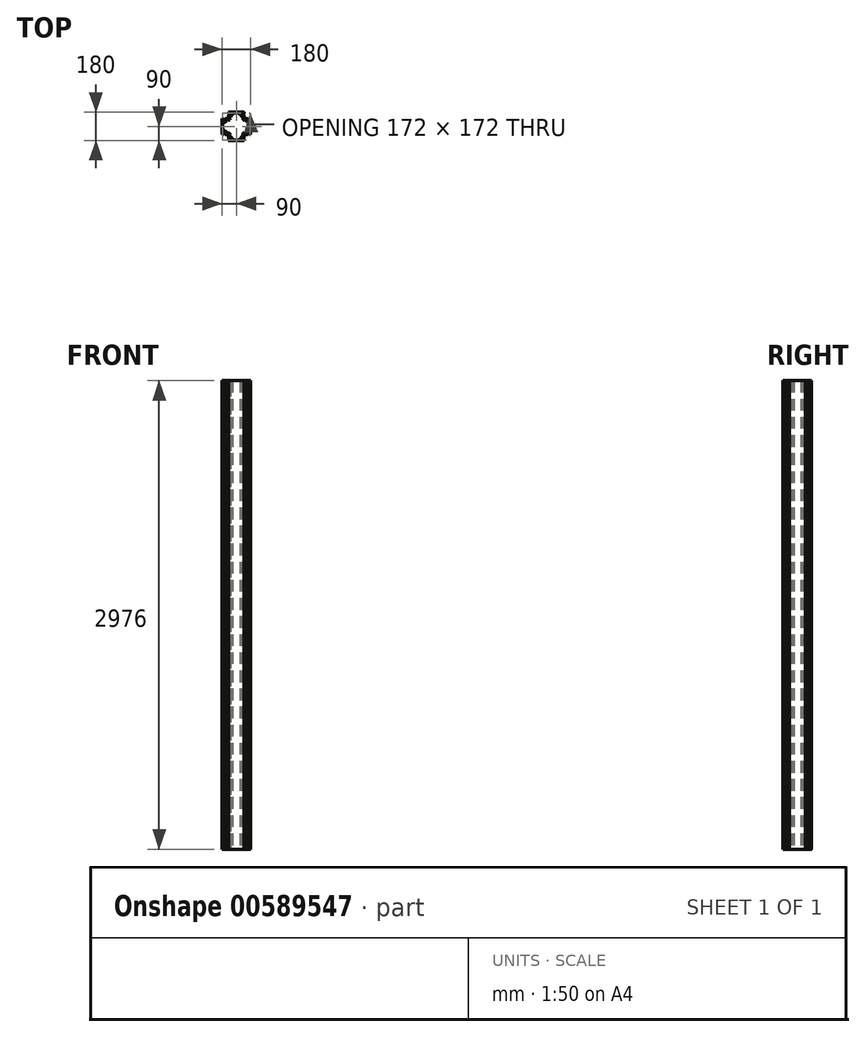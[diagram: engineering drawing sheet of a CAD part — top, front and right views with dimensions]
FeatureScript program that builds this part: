
annotation { "Feature Type Name" : "Feature", "Feature Type Description" : "" }
export const myFeature = defineFeature(function(context is Context, id is Id, definition is map)
    precondition{}
    {
        {
            var Q0;
            Q0=qCreatedBy(makeId("Top.planeOp"),FACE);
            var sketch = newSketch(context, id + "F0", { "sketchPlane" : qUnion([Q0])});
            skLineSegment(sketch, "E0", {"start": v(-58.4, 0) * mm, "end": v(68.52, 0) * mm, "construction": true});
            skLineSegment(sketch, "E1", {"start": v(0, 55.81) * mm, "end": v(0, -52.18) * mm, "construction": true});
            skLineSegment(sketch, "E2.bottom", {"start": v(-50, 90) * mm, "end": v(50, 90) * mm});
            skLineSegment(sketch, "E2.top", {"start": v(-50, -90) * mm, "end": v(50, -90) * mm});
            skLineSegment(sketch, "E2.left", {"start": v(-90, 50) * mm, "end": v(-90, -50) * mm});
            skLineSegment(sketch, "E2.right", {"start": v(90, 50) * mm, "end": v(90, -50) * mm});
            skLineSegment(sketch, "E3", {"start": v(-90, 50) * mm, "end": v(-82, 50) * mm});
            skLineSegment(sketch, "E4", {"start": v(-50, 50) * mm, "end": v(-50, 72) * mm});
            skLineSegment(sketch, "E5.MirrorCS", {"start": v(90, 50) * mm, "end": v(82, 50) * mm});
            skLineSegment(sketch, "E6.MirrorCS", {"start": v(50, 50) * mm, "end": v(50, 72) * mm});
            skLineSegment(sketch, "E7.MirrorCS", {"start": v(50, -50) * mm, "end": v(50, -72) * mm});
            skLineSegment(sketch, "E8.MirrorCS", {"start": v(90, -50) * mm, "end": v(82, -50) * mm});
            skLineSegment(sketch, "E9.MirrorCS", {"start": v(-50, -50) * mm, "end": v(-50, -72) * mm});
            skLineSegment(sketch, "E10.MirrorCS", {"start": v(-90, -50) * mm, "end": v(-82, -50) * mm});
            skLineSegment(sketch, "E11", {"start": v(-82, -50) * mm, "end": v(-82, -46) * mm});
            skLineSegment(sketch, "E12", {"start": v(-82, -46) * mm, "end": v(-86, -46) * mm});
            skLineSegment(sketch, "E13", {"start": v(-86, -46) * mm, "end": v(-86, -38) * mm});
            skLineSegment(sketch, "E14", {"start": v(-86, -38) * mm, "end": v(-68, -38) * mm});
            skLineSegment(sketch, "E15", {"start": v(-68, -38) * mm, "end": v(-68, -46) * mm});
            skLineSegment(sketch, "E16", {"start": v(-68, -46) * mm, "end": v(-72, -46) * mm});
            skLineSegment(sketch, "E17", {"start": v(-72, -46) * mm, "end": v(-72, -50) * mm});
            skLineSegment(sketch, "E18.MirrorCS", {"start": v(-68, 46) * mm, "end": v(-72, 46) * mm});
            skLineSegment(sketch, "E19.MirrorCS", {"start": v(-86, 38) * mm, "end": v(-68, 38) * mm});
            skLineSegment(sketch, "E20.MirrorCS", {"start": v(-82, 50) * mm, "end": v(-82, 46) * mm});
            skLineSegment(sketch, "E21.MirrorCS", {"start": v(-86, 46) * mm, "end": v(-86, 38) * mm});
            skLineSegment(sketch, "E22.MirrorCS", {"start": v(-82, 46) * mm, "end": v(-86, 46) * mm});
            skLineSegment(sketch, "E23.MirrorCS", {"start": v(-68, 38) * mm, "end": v(-68, 46) * mm});
            skLineSegment(sketch, "E24.MirrorCS", {"start": v(-72, 46) * mm, "end": v(-72, 50) * mm});
            skLineSegment(sketch, "E25.MirrorCS", {"start": v(68, -38) * mm, "end": v(68, -46) * mm});
            skLineSegment(sketch, "E26.MirrorCS", {"start": v(86, 38) * mm, "end": v(68, 38) * mm});
            skLineSegment(sketch, "E27.MirrorCS", {"start": v(82, 46) * mm, "end": v(86, 46) * mm});
            skLineSegment(sketch, "E28.MirrorCS", {"start": v(86, -38) * mm, "end": v(68, -38) * mm});
            skLineSegment(sketch, "E29.MirrorCS", {"start": v(68, 46) * mm, "end": v(72, 46) * mm});
            skLineSegment(sketch, "E30.MirrorCS", {"start": v(86, 46) * mm, "end": v(86, 38) * mm});
            skLineSegment(sketch, "E31.MirrorCS", {"start": v(86, -46) * mm, "end": v(86, -38) * mm});
            skLineSegment(sketch, "E32.MirrorCS", {"start": v(72, -46) * mm, "end": v(72, -50) * mm});
            skLineSegment(sketch, "E33.MirrorCS", {"start": v(82, 50) * mm, "end": v(82, 46) * mm});
            skLineSegment(sketch, "E34.MirrorCS", {"start": v(72, 46) * mm, "end": v(72, 50) * mm});
            skLineSegment(sketch, "E35.MirrorCS", {"start": v(68, 38) * mm, "end": v(68, 46) * mm});
            skLineSegment(sketch, "E36.MirrorCS", {"start": v(82, -50) * mm, "end": v(82, -46) * mm});
            skLineSegment(sketch, "E37.MirrorCS", {"start": v(68, -46) * mm, "end": v(72, -46) * mm});
            skLineSegment(sketch, "E38.MirrorCS", {"start": v(82, -46) * mm, "end": v(86, -46) * mm});
            skLineSegment(sketch, "E39", {"start": v(-50, 50) * mm, "end": v(0, 0) * mm, "construction": true});
            skLineSegment(sketch, "E40.MirrorCS", {"start": v(-38, 68) * mm, "end": v(-46, 68) * mm});
            skLineSegment(sketch, "E41.MirrorCS", {"start": v(-46, 68) * mm, "end": v(-46, 72) * mm});
            skLineSegment(sketch, "E42.MirrorCS", {"start": v(-46, 72) * mm, "end": v(-50, 72) * mm});
            skLineSegment(sketch, "E43.MirrorCS", {"start": v(-38, 86) * mm, "end": v(-38, 68) * mm});
            skLineSegment(sketch, "E44.MirrorCS", {"start": v(-46, 86) * mm, "end": v(-38, 86) * mm});
            skLineSegment(sketch, "E45.MirrorCS", {"start": v(-50, 82) * mm, "end": v(-46, 82) * mm});
            skLineSegment(sketch, "E46.MirrorCS", {"start": v(-46, 82) * mm, "end": v(-46, 86) * mm});
            skLineSegment(sketch, "E47.MirrorCS", {"start": v(46, 82) * mm, "end": v(46, 86) * mm});
            skLineSegment(sketch, "E48.MirrorCS", {"start": v(38, 86) * mm, "end": v(38, 68) * mm});
            skLineSegment(sketch, "E49.MirrorCS", {"start": v(46, 68) * mm, "end": v(46, 72) * mm});
            skLineSegment(sketch, "E50.MirrorCS", {"start": v(50, 82) * mm, "end": v(46, 82) * mm});
            skLineSegment(sketch, "E51.MirrorCS", {"start": v(46, 86) * mm, "end": v(38, 86) * mm});
            skLineSegment(sketch, "E52.MirrorCS", {"start": v(38, 68) * mm, "end": v(46, 68) * mm});
            skLineSegment(sketch, "E53.MirrorCS", {"start": v(46, 72) * mm, "end": v(50, 72) * mm});
            skLineSegment(sketch, "E54.MirrorCS", {"start": v(-46, -86) * mm, "end": v(-38, -86) * mm});
            skLineSegment(sketch, "E55.MirrorCS", {"start": v(50, -82) * mm, "end": v(46, -82) * mm});
            skLineSegment(sketch, "E56.MirrorCS", {"start": v(-38, -86) * mm, "end": v(-38, -68) * mm});
            skLineSegment(sketch, "E57.MirrorCS", {"start": v(-46, -82) * mm, "end": v(-46, -86) * mm});
            skLineSegment(sketch, "E58.MirrorCS", {"start": v(-38, -68) * mm, "end": v(-46, -68) * mm});
            skLineSegment(sketch, "E59.MirrorCS", {"start": v(38, -86) * mm, "end": v(38, -68) * mm});
            skLineSegment(sketch, "E60.MirrorCS", {"start": v(-50, -82) * mm, "end": v(-46, -82) * mm});
            skLineSegment(sketch, "E61.MirrorCS", {"start": v(-46, -72) * mm, "end": v(-50, -72) * mm});
            skLineSegment(sketch, "E62.MirrorCS", {"start": v(-46, -68) * mm, "end": v(-46, -72) * mm});
            skLineSegment(sketch, "E63.MirrorCS", {"start": v(46, -72) * mm, "end": v(50, -72) * mm});
            skLineSegment(sketch, "E64.MirrorCS", {"start": v(38, -68) * mm, "end": v(46, -68) * mm});
            skLineSegment(sketch, "E65.MirrorCS", {"start": v(46, -68) * mm, "end": v(46, -72) * mm});
            skLineSegment(sketch, "E66.MirrorCS", {"start": v(46, -82) * mm, "end": v(46, -86) * mm});
            skLineSegment(sketch, "E67.MirrorCS", {"start": v(46, -86) * mm, "end": v(38, -86) * mm});
            skLineSegment(sketch, "E68.trimOffspring", {"start": v(-72, 50) * mm, "end": v(-50, 50) * mm});
            skLineSegment(sketch, "E69.trimOffspring", {"start": v(-50, 82) * mm, "end": v(-50, 90) * mm});
            skLineSegment(sketch, "E70.trimOffspring", {"start": v(50, 82) * mm, "end": v(50, 90) * mm});
            skLineSegment(sketch, "E71.trimOffspring", {"start": v(72, 50) * mm, "end": v(50, 50) * mm});
            skLineSegment(sketch, "E72.trimOffspring", {"start": v(72, -50) * mm, "end": v(50, -50) * mm});
            skLineSegment(sketch, "E73.trimOffspring", {"start": v(50, -82) * mm, "end": v(50, -90) * mm});
            skLineSegment(sketch, "E74.trimOffspring", {"start": v(-50, -82) * mm, "end": v(-50, -90) * mm});
            skLineSegment(sketch, "E75.trimOffspring", {"start": v(-72, -50) * mm, "end": v(-50, -50) * mm});
            skSolve(sketch);
        }
        {
            var Q0;
            Q0=qSketchRegion(id+"F0",true);
            extrude(context, id + "F1", {"entities" : qUnion([Q0]), "depth" : 2976 * mm, "offsetDistance" : 25 * mm});
        }
        {
            var Q0;
            Q0=makeQuery(id+"F1.opExtrude","CAP_FACE",FACE,{"disambiguationData":[OSD([sQuery(id+"F0.wireOp",EDGE,"E2.bottom"),sQuery(id+"F0.wireOp",EDGE,"E2.top"),sQuery(id+"F0.wireOp",EDGE,"E2.left"),sQuery(id+"F0.wireOp",EDGE,"E2.right"),sQuery(id+"F0.wireOp",EDGE,"E3"),sQuery(id+"F0.wireOp",EDGE,"E4"),sQuery(id+"F0.wireOp",EDGE,"E5.MirrorCS"),sQuery(id+"F0.wireOp",EDGE,"E6.MirrorCS"),sQuery(id+"F0.wireOp",EDGE,"E7.MirrorCS"),sQuery(id+"F0.wireOp",EDGE,"E8.MirrorCS"),sQuery(id+"F0.wireOp",EDGE,"E9.MirrorCS"),sQuery(id+"F0.wireOp",EDGE,"E10.MirrorCS")])],"isStart":false});
            var Q1;
            Q1=makeQuery(id+"F1.opExtrude","CAP_FACE",FACE,{"disambiguationData":[OSD([sQuery(id+"F0.wireOp",EDGE,"E2.bottom"),sQuery(id+"F0.wireOp",EDGE,"E2.top"),sQuery(id+"F0.wireOp",EDGE,"E2.left"),sQuery(id+"F0.wireOp",EDGE,"E2.right"),sQuery(id+"F0.wireOp",EDGE,"E3"),sQuery(id+"F0.wireOp",EDGE,"E4"),sQuery(id+"F0.wireOp",EDGE,"E5.MirrorCS"),sQuery(id+"F0.wireOp",EDGE,"E6.MirrorCS"),sQuery(id+"F0.wireOp",EDGE,"E7.MirrorCS"),sQuery(id+"F0.wireOp",EDGE,"E8.MirrorCS"),sQuery(id+"F0.wireOp",EDGE,"E9.MirrorCS"),sQuery(id+"F0.wireOp",EDGE,"E10.MirrorCS")])],"isStart":true});
            shell(context, id + "F2", {"entities" : qUnion([Q0, Q1]), "thickness" : 4 * mm});
        }
        {
            var Q0;
            Q0=makeQuery(id+"F1.opExtrude","SWEPT_EDGE",EDGE,{"disambiguationData":[OSD([sQuery(id+"F0.wireOp",EDGE,"E2.top"),sQuery(id+"F0.wireOp",EDGE,"E74.trimOffspring")])]});
            var Q1;
            Q1=makeQuery(id+"F1.opExtrude","SWEPT_EDGE",EDGE,{"disambiguationData":[OSD([sQuery(id+"F0.wireOp",EDGE,"E2.left"),sQuery(id+"F0.wireOp",EDGE,"E10.MirrorCS")])]});
            var Q2;
            Q2=makeQuery(id+"F1.opExtrude","SWEPT_EDGE",EDGE,{"disambiguationData":[OSD([sQuery(id+"F0.wireOp",EDGE,"E2.top"),sQuery(id+"F0.wireOp",EDGE,"E73.trimOffspring")])]});
            var Q3;
            Q3=makeQuery(id+"F1.opExtrude","SWEPT_EDGE",EDGE,{"disambiguationData":[OSD([sQuery(id+"F0.wireOp",EDGE,"E2.right"),sQuery(id+"F0.wireOp",EDGE,"E8.MirrorCS")])]});
            var Q4;
            Q4=makeQuery(id+"F1.opExtrude","SWEPT_EDGE",EDGE,{"disambiguationData":[OSD([sQuery(id+"F0.wireOp",EDGE,"E2.right"),sQuery(id+"F0.wireOp",EDGE,"E5.MirrorCS")])]});
            var Q5;
            Q5=makeQuery(id+"F1.opExtrude","SWEPT_EDGE",EDGE,{"disambiguationData":[OSD([sQuery(id+"F0.wireOp",EDGE,"E2.bottom"),sQuery(id+"F0.wireOp",EDGE,"E70.trimOffspring")])]});
            var Q6;
            Q6=makeQuery(id+"F1.opExtrude","SWEPT_EDGE",EDGE,{"disambiguationData":[OSD([sQuery(id+"F0.wireOp",EDGE,"E2.bottom"),sQuery(id+"F0.wireOp",EDGE,"E69.trimOffspring")])]});
            var Q7;
            Q7=makeQuery(id+"F1.opExtrude","SWEPT_EDGE",EDGE,{"disambiguationData":[OSD([sQuery(id+"F0.wireOp",EDGE,"E2.left"),sQuery(id+"F0.wireOp",EDGE,"E3")])]});
            fillet(context, id + "F3", {"entities" : qUnion([Q0, Q1, Q2, Q3, Q4, Q5, Q6, Q7]), "radius" : 3 * mm, "tangentPropagation" : true, "allowEdgeOverflow" : false});
        }
        {
            var Q0;
            Q0=makeQuery(id+"F1.opExtrude","CAP_FACE",FACE,{"disambiguationData":[OSD([sQuery(id+"F0.wireOp",EDGE,"E2.bottom"),sQuery(id+"F0.wireOp",EDGE,"E2.top"),sQuery(id+"F0.wireOp",EDGE,"E2.left"),sQuery(id+"F0.wireOp",EDGE,"E2.right"),sQuery(id+"F0.wireOp",EDGE,"E3"),sQuery(id+"F0.wireOp",EDGE,"E4"),sQuery(id+"F0.wireOp",EDGE,"E5.MirrorCS"),sQuery(id+"F0.wireOp",EDGE,"E6.MirrorCS"),sQuery(id+"F0.wireOp",EDGE,"E7.MirrorCS"),sQuery(id+"F0.wireOp",EDGE,"E8.MirrorCS"),sQuery(id+"F0.wireOp",EDGE,"E9.MirrorCS"),sQuery(id+"F0.wireOp",EDGE,"E10.MirrorCS"),sQuery(id+"F0.wireOp",EDGE,"E11"),sQuery(id+"F0.wireOp",EDGE,"E12"),sQuery(id+"F0.wireOp",EDGE,"E13"),sQuery(id+"F0.wireOp",EDGE,"E14"),sQuery(id+"F0.wireOp",EDGE,"E15"),sQuery(id+"F0.wireOp",EDGE,"E16"),sQuery(id+"F0.wireOp",EDGE,"E17"),sQuery(id+"F0.wireOp",EDGE,"E18.MirrorCS"),sQuery(id+"F0.wireOp",EDGE,"E19.MirrorCS"),sQuery(id+"F0.wireOp",EDGE,"E20.MirrorCS"),sQuery(id+"F0.wireOp",EDGE,"E21.MirrorCS"),sQuery(id+"F0.wireOp",EDGE,"E22.MirrorCS"),sQuery(id+"F0.wireOp",EDGE,"E23.MirrorCS"),sQuery(id+"F0.wireOp",EDGE,"E24.MirrorCS"),sQuery(id+"F0.wireOp",EDGE,"E25.MirrorCS"),sQuery(id+"F0.wireOp",EDGE,"E26.MirrorCS"),sQuery(id+"F0.wireOp",EDGE,"E27.MirrorCS"),sQuery(id+"F0.wireOp",EDGE,"E28.MirrorCS"),sQuery(id+"F0.wireOp",EDGE,"E29.MirrorCS"),sQuery(id+"F0.wireOp",EDGE,"E30.MirrorCS"),sQuery(id+"F0.wireOp",EDGE,"E31.MirrorCS"),sQuery(id+"F0.wireOp",EDGE,"E32.MirrorCS"),sQuery(id+"F0.wireOp",EDGE,"E33.MirrorCS"),sQuery(id+"F0.wireOp",EDGE,"E34.MirrorCS"),sQuery(id+"F0.wireOp",EDGE,"E35.MirrorCS"),sQuery(id+"F0.wireOp",EDGE,"E36.MirrorCS"),sQuery(id+"F0.wireOp",EDGE,"E37.MirrorCS"),sQuery(id+"F0.wireOp",EDGE,"E38.MirrorCS"),sQuery(id+"F0.wireOp",EDGE,"E40.MirrorCS"),sQuery(id+"F0.wireOp",EDGE,"E41.MirrorCS"),sQuery(id+"F0.wireOp",EDGE,"E42.MirrorCS"),sQuery(id+"F0.wireOp",EDGE,"E43.MirrorCS"),sQuery(id+"F0.wireOp",EDGE,"E44.MirrorCS"),sQuery(id+"F0.wireOp",EDGE,"E45.MirrorCS"),sQuery(id+"F0.wireOp",EDGE,"E46.MirrorCS"),sQuery(id+"F0.wireOp",EDGE,"E47.MirrorCS"),sQuery(id+"F0.wireOp",EDGE,"E48.MirrorCS"),sQuery(id+"F0.wireOp",EDGE,"E49.MirrorCS"),sQuery(id+"F0.wireOp",EDGE,"E50.MirrorCS"),sQuery(id+"F0.wireOp",EDGE,"E51.MirrorCS"),sQuery(id+"F0.wireOp",EDGE,"E52.MirrorCS"),sQuery(id+"F0.wireOp",EDGE,"E53.MirrorCS"),sQuery(id+"F0.wireOp",EDGE,"E54.MirrorCS"),sQuery(id+"F0.wireOp",EDGE,"E55.MirrorCS"),sQuery(id+"F0.wireOp",EDGE,"E56.MirrorCS"),sQuery(id+"F0.wireOp",EDGE,"E57.MirrorCS"),sQuery(id+"F0.wireOp",EDGE,"E58.MirrorCS"),sQuery(id+"F0.wireOp",EDGE,"E59.MirrorCS"),sQuery(id+"F0.wireOp",EDGE,"E60.MirrorCS"),sQuery(id+"F0.wireOp",EDGE,"E61.MirrorCS"),sQuery(id+"F0.wireOp",EDGE,"E62.MirrorCS"),sQuery(id+"F0.wireOp",EDGE,"E63.MirrorCS"),sQuery(id+"F0.wireOp",EDGE,"E64.MirrorCS"),sQuery(id+"F0.wireOp",EDGE,"E65.MirrorCS"),sQuery(id+"F0.wireOp",EDGE,"E66.MirrorCS"),sQuery(id+"F0.wireOp",EDGE,"E67.MirrorCS"),sQuery(id+"F0.wireOp",EDGE,"E68.trimOffspring"),sQuery(id+"F0.wireOp",EDGE,"E69.trimOffspring"),sQuery(id+"F0.wireOp",EDGE,"E70.trimOffspring"),sQuery(id+"F0.wireOp",EDGE,"E71.trimOffspring"),sQuery(id+"F0.wireOp",EDGE,"E72.trimOffspring"),sQuery(id+"F0.wireOp",EDGE,"E73.trimOffspring"),sQuery(id+"F0.wireOp",EDGE,"E74.trimOffspring"),sQuery(id+"F0.wireOp",EDGE,"E75.trimOffspring")])],"isStart":true});
            var sketch = newSketch(context, id + "F4", { "sketchPlane" : qUnion([Q0])});
            skLineSegment(sketch, "E76.bottom", {"start": v(-64, 38) * mm, "end": v(-61, 38) * mm});
            skLineSegment(sketch, "E76.top", {"start": v(-64, 34) * mm, "end": v(-61, 34) * mm});
            skLineSegment(sketch, "E76.left", {"start": v(-64, 38) * mm, "end": v(-64, 34) * mm});
            skLineSegment(sketch, "E76.right", {"start": v(-61, 38) * mm, "end": v(-61, 34) * mm});
            skLineSegment(sketch, "E77", {"start": v(-74, 34) * mm, "end": v(-74, 23) * mm});
            skLineSegment(sketch, "E78", {"start": v(-74, 23) * mm, "end": v(-78, 23) * mm});
            skLineSegment(sketch, "E79", {"start": v(-78, 23) * mm, "end": v(-78, 34) * mm});
            skLineSegment(sketch, "E80", {"start": v(-78, 34) * mm, "end": v(-74, 34) * mm});
            skLineSegment(sketch, "E81", {"start": v(0, 86) * mm, "end": v(0, 0) * mm, "construction": true});
            skLineSegment(sketch, "E82", {"start": v(0, 0) * mm, "end": v(-86, 0) * mm, "construction": true});
            skLineSegment(sketch, "E83.MirrorCS", {"start": v(64, 38) * mm, "end": v(64, 34) * mm});
            skLineSegment(sketch, "E84.MirrorCS", {"start": v(61, 38) * mm, "end": v(61, 34) * mm});
            skLineSegment(sketch, "E85.MirrorCS", {"start": v(78, 34) * mm, "end": v(74, 34) * mm});
            skLineSegment(sketch, "E86.MirrorCS", {"start": v(74, 23) * mm, "end": v(78, 23) * mm});
            skLineSegment(sketch, "E87.MirrorCS", {"start": v(64, 38) * mm, "end": v(61, 38) * mm});
            skLineSegment(sketch, "E88.MirrorCS", {"start": v(64, 34) * mm, "end": v(61, 34) * mm});
            skLineSegment(sketch, "E89.MirrorCS", {"start": v(78, 23) * mm, "end": v(78, 34) * mm});
            skLineSegment(sketch, "E90.MirrorCS", {"start": v(74, 34) * mm, "end": v(74, 23) * mm});
            skLineSegment(sketch, "E91.MirrorCS", {"start": v(0, 0) * mm, "end": v(86, 0) * mm, "construction": true});
            skLineSegment(sketch, "E92.MirrorCS", {"start": v(74, -34) * mm, "end": v(74, -23) * mm});
            skLineSegment(sketch, "E93.MirrorCS", {"start": v(74, -23) * mm, "end": v(78, -23) * mm});
            skLineSegment(sketch, "E94.MirrorCS", {"start": v(64, -38) * mm, "end": v(61, -38) * mm});
            skLineSegment(sketch, "E95.MirrorCS", {"start": v(64, -34) * mm, "end": v(61, -34) * mm});
            skLineSegment(sketch, "E96.MirrorCS", {"start": v(-64, -38) * mm, "end": v(-61, -38) * mm});
            skLineSegment(sketch, "E97.MirrorCS", {"start": v(-64, -34) * mm, "end": v(-61, -34) * mm});
            skLineSegment(sketch, "E98.MirrorCS", {"start": v(-64, -38) * mm, "end": v(-64, -34) * mm});
            skLineSegment(sketch, "E99.MirrorCS", {"start": v(-61, -38) * mm, "end": v(-61, -34) * mm});
            skLineSegment(sketch, "E100.MirrorCS", {"start": v(-74, -34) * mm, "end": v(-74, -23) * mm});
            skLineSegment(sketch, "E101.MirrorCS", {"start": v(-74, -23) * mm, "end": v(-78, -23) * mm});
            skLineSegment(sketch, "E102.MirrorCS", {"start": v(78, -34) * mm, "end": v(74, -34) * mm});
            skLineSegment(sketch, "E103.MirrorCS", {"start": v(61, -38) * mm, "end": v(61, -34) * mm});
            skLineSegment(sketch, "E104.MirrorCS", {"start": v(78, -23) * mm, "end": v(78, -34) * mm});
            skLineSegment(sketch, "E105.MirrorCS", {"start": v(-78, -34) * mm, "end": v(-74, -34) * mm});
            skLineSegment(sketch, "E106.MirrorCS", {"start": v(-78, -23) * mm, "end": v(-78, -34) * mm});
            skLineSegment(sketch, "E107.MirrorCS", {"start": v(64, -38) * mm, "end": v(64, -34) * mm});
            skLineSegment(sketch, "E108", {"start": v(-46, 46) * mm, "end": v(0, 0) * mm, "construction": true});
            skLineSegment(sketch, "E109.MirrorCS", {"start": v(-34, 78) * mm, "end": v(-34, 74) * mm});
            skLineSegment(sketch, "E110.MirrorCS", {"start": v(-23, 78) * mm, "end": v(-34, 78) * mm});
            skLineSegment(sketch, "E111.MirrorCS", {"start": v(-23, 74) * mm, "end": v(-23, 78) * mm});
            skLineSegment(sketch, "E112.MirrorCS", {"start": v(-34, 74) * mm, "end": v(-23, 74) * mm});
            skLineSegment(sketch, "E113.MirrorCS", {"start": v(-38, 61) * mm, "end": v(-34, 61) * mm});
            skLineSegment(sketch, "E114.MirrorCS", {"start": v(-38, 64) * mm, "end": v(-34, 64) * mm});
            skLineSegment(sketch, "E115.MirrorCS", {"start": v(-38, 64) * mm, "end": v(-38, 61) * mm});
            skLineSegment(sketch, "E116.MirrorCS", {"start": v(-34, 64) * mm, "end": v(-34, 61) * mm});
            skLineSegment(sketch, "E117.MirrorCS", {"start": v(34, 78) * mm, "end": v(34, 74) * mm});
            skLineSegment(sketch, "E118.MirrorCS", {"start": v(34, 64) * mm, "end": v(34, 61) * mm});
            skLineSegment(sketch, "E119.MirrorCS", {"start": v(23, 78) * mm, "end": v(34, 78) * mm});
            skLineSegment(sketch, "E120.MirrorCS", {"start": v(23, 74) * mm, "end": v(23, 78) * mm});
            skLineSegment(sketch, "E121.MirrorCS", {"start": v(34, 74) * mm, "end": v(23, 74) * mm});
            skLineSegment(sketch, "E122.MirrorCS", {"start": v(38, 61) * mm, "end": v(34, 61) * mm});
            skLineSegment(sketch, "E123.MirrorCS", {"start": v(38, 64) * mm, "end": v(38, 61) * mm});
            skLineSegment(sketch, "E124.MirrorCS", {"start": v(38, 64) * mm, "end": v(34, 64) * mm});
            skLineSegment(sketch, "E125.MirrorCS", {"start": v(-34, -78) * mm, "end": v(-34, -74) * mm});
            skLineSegment(sketch, "E126.MirrorCS", {"start": v(34, -64) * mm, "end": v(34, -61) * mm});
            skLineSegment(sketch, "E127.MirrorCS", {"start": v(-34, -64) * mm, "end": v(-34, -61) * mm});
            skLineSegment(sketch, "E128.MirrorCS", {"start": v(34, -78) * mm, "end": v(34, -74) * mm});
            skLineSegment(sketch, "E129.MirrorCS", {"start": v(-23, -78) * mm, "end": v(-34, -78) * mm});
            skLineSegment(sketch, "E130.MirrorCS", {"start": v(23, -78) * mm, "end": v(34, -78) * mm});
            skLineSegment(sketch, "E131.MirrorCS", {"start": v(23, -74) * mm, "end": v(23, -78) * mm});
            skLineSegment(sketch, "E132.MirrorCS", {"start": v(-23, -74) * mm, "end": v(-23, -78) * mm});
            skLineSegment(sketch, "E133.MirrorCS", {"start": v(38, -64) * mm, "end": v(34, -64) * mm});
            skLineSegment(sketch, "E134.MirrorCS", {"start": v(38, -64) * mm, "end": v(38, -61) * mm});
            skLineSegment(sketch, "E135.MirrorCS", {"start": v(-38, -64) * mm, "end": v(-34, -64) * mm});
            skLineSegment(sketch, "E136.MirrorCS", {"start": v(34, -74) * mm, "end": v(23, -74) * mm});
            skLineSegment(sketch, "E137.MirrorCS", {"start": v(38, -61) * mm, "end": v(34, -61) * mm});
            skLineSegment(sketch, "E138.MirrorCS", {"start": v(-38, -61) * mm, "end": v(-34, -61) * mm});
            skLineSegment(sketch, "E139.MirrorCS", {"start": v(-34, -74) * mm, "end": v(-23, -74) * mm});
            skLineSegment(sketch, "E140.MirrorCS", {"start": v(-38, -64) * mm, "end": v(-38, -61) * mm});
            skArc(sketch, "E141", {"start": v(-45.65, -43.53) * mm, "mid": v(-47.77, -47.77) * mm, "end": v(-43.53, -45.65) * mm});
            skArc(sketch, "E142.0", {"start": v(-43.69, -41.57) * mm, "mid": v(-49.54, -49.54) * mm, "end": v(-41.57, -43.69) * mm});
            skLineSegment(sketch, "E143", {"start": v(-46, -46) * mm, "end": v(-44.23, -44.23) * mm, "construction": true});
            skLineSegment(sketch, "E144", {"start": v(-45.65, -43.53) * mm, "end": v(-43.53, -45.65) * mm, "construction": true});
            skLineSegment(sketch, "E145", {"start": v(-45.65, -43.53) * mm, "end": v(-43.69, -41.57) * mm});
            skLineSegment(sketch, "E146", {"start": v(-43.53, -45.65) * mm, "end": v(-41.57, -43.69) * mm});
            skLineSegment(sketch, "E147.MirrorCS", {"start": v(46, -46) * mm, "end": v(44.23, -44.23) * mm, "construction": true});
            skLineSegment(sketch, "E148.MirrorCS", {"start": v(45.65, -43.53) * mm, "end": v(43.53, -45.65) * mm, "construction": true});
            skArc(sketch, "E149.MirrorCS", {"start": v(43.69, -41.57) * mm, "mid": v(49.54, -49.54) * mm, "end": v(41.57, -43.69) * mm});
            skArc(sketch, "E150.MirrorCS", {"start": v(45.65, -43.53) * mm, "mid": v(47.77, -47.77) * mm, "end": v(43.53, -45.65) * mm});
            skLineSegment(sketch, "E151.MirrorCS", {"start": v(43.53, -45.65) * mm, "end": v(41.57, -43.69) * mm});
            skLineSegment(sketch, "E152.MirrorCS", {"start": v(45.65, -43.53) * mm, "end": v(43.69, -41.57) * mm});
            skLineSegment(sketch, "E153.MirrorCS", {"start": v(46, 46) * mm, "end": v(44.23, 44.23) * mm, "construction": true});
            skLineSegment(sketch, "E154.MirrorCS", {"start": v(45.65, 43.53) * mm, "end": v(43.53, 45.65) * mm, "construction": true});
            skLineSegment(sketch, "E155.MirrorCS", {"start": v(43.53, 45.65) * mm, "end": v(41.57, 43.69) * mm});
            skLineSegment(sketch, "E156.MirrorCS", {"start": v(45.65, 43.53) * mm, "end": v(43.69, 41.57) * mm});
            skLineSegment(sketch, "E157.MirrorCS", {"start": v(-46, 46) * mm, "end": v(-44.23, 44.23) * mm, "construction": true});
            skLineSegment(sketch, "E158.MirrorCS", {"start": v(-45.65, 43.53) * mm, "end": v(-43.53, 45.65) * mm, "construction": true});
            skLineSegment(sketch, "E159.MirrorCS", {"start": v(-45.65, 43.53) * mm, "end": v(-43.69, 41.57) * mm});
            skLineSegment(sketch, "E160.MirrorCS", {"start": v(-43.53, 45.65) * mm, "end": v(-41.57, 43.69) * mm});
            skArc(sketch, "E161.MirrorCS", {"start": v(43.69, 41.57) * mm, "mid": v(49.54, 49.54) * mm, "end": v(41.57, 43.69) * mm});
            skArc(sketch, "E162.MirrorCS", {"start": v(45.65, 43.53) * mm, "mid": v(47.77, 47.77) * mm, "end": v(43.53, 45.65) * mm});
            skArc(sketch, "E163.MirrorCS", {"start": v(-43.69, 41.57) * mm, "mid": v(-49.54, 49.54) * mm, "end": v(-41.57, 43.69) * mm});
            skArc(sketch, "E164.MirrorCS", {"start": v(-45.65, 43.53) * mm, "mid": v(-47.77, 47.77) * mm, "end": v(-43.53, 45.65) * mm});
            skSolve(sketch);
        }
        {
            var Q0;
            Q0=qSketchRegion(id+"F4",true);
            var Q1;
            Q1=makeQuery(id+"F1.opExtrude","CAP_FACE",FACE,{"disambiguationData":[OSD([sQuery(id+"F0.wireOp",EDGE,"E2.bottom"),sQuery(id+"F0.wireOp",EDGE,"E2.top"),sQuery(id+"F0.wireOp",EDGE,"E2.left"),sQuery(id+"F0.wireOp",EDGE,"E2.right"),sQuery(id+"F0.wireOp",EDGE,"E3"),sQuery(id+"F0.wireOp",EDGE,"E4"),sQuery(id+"F0.wireOp",EDGE,"E5.MirrorCS"),sQuery(id+"F0.wireOp",EDGE,"E6.MirrorCS"),sQuery(id+"F0.wireOp",EDGE,"E7.MirrorCS"),sQuery(id+"F0.wireOp",EDGE,"E8.MirrorCS"),sQuery(id+"F0.wireOp",EDGE,"E9.MirrorCS"),sQuery(id+"F0.wireOp",EDGE,"E10.MirrorCS"),sQuery(id+"F0.wireOp",EDGE,"E11"),sQuery(id+"F0.wireOp",EDGE,"E12"),sQuery(id+"F0.wireOp",EDGE,"E13"),sQuery(id+"F0.wireOp",EDGE,"E14"),sQuery(id+"F0.wireOp",EDGE,"E15"),sQuery(id+"F0.wireOp",EDGE,"E16"),sQuery(id+"F0.wireOp",EDGE,"E17"),sQuery(id+"F0.wireOp",EDGE,"E18.MirrorCS"),sQuery(id+"F0.wireOp",EDGE,"E19.MirrorCS"),sQuery(id+"F0.wireOp",EDGE,"E20.MirrorCS"),sQuery(id+"F0.wireOp",EDGE,"E21.MirrorCS"),sQuery(id+"F0.wireOp",EDGE,"E22.MirrorCS"),sQuery(id+"F0.wireOp",EDGE,"E23.MirrorCS"),sQuery(id+"F0.wireOp",EDGE,"E24.MirrorCS"),sQuery(id+"F0.wireOp",EDGE,"E25.MirrorCS"),sQuery(id+"F0.wireOp",EDGE,"E26.MirrorCS"),sQuery(id+"F0.wireOp",EDGE,"E27.MirrorCS"),sQuery(id+"F0.wireOp",EDGE,"E28.MirrorCS"),sQuery(id+"F0.wireOp",EDGE,"E29.MirrorCS"),sQuery(id+"F0.wireOp",EDGE,"E30.MirrorCS"),sQuery(id+"F0.wireOp",EDGE,"E31.MirrorCS"),sQuery(id+"F0.wireOp",EDGE,"E32.MirrorCS"),sQuery(id+"F0.wireOp",EDGE,"E33.MirrorCS"),sQuery(id+"F0.wireOp",EDGE,"E34.MirrorCS"),sQuery(id+"F0.wireOp",EDGE,"E35.MirrorCS"),sQuery(id+"F0.wireOp",EDGE,"E36.MirrorCS"),sQuery(id+"F0.wireOp",EDGE,"E37.MirrorCS"),sQuery(id+"F0.wireOp",EDGE,"E38.MirrorCS"),sQuery(id+"F0.wireOp",EDGE,"E40.MirrorCS"),sQuery(id+"F0.wireOp",EDGE,"E41.MirrorCS"),sQuery(id+"F0.wireOp",EDGE,"E42.MirrorCS"),sQuery(id+"F0.wireOp",EDGE,"E43.MirrorCS"),sQuery(id+"F0.wireOp",EDGE,"E44.MirrorCS"),sQuery(id+"F0.wireOp",EDGE,"E45.MirrorCS"),sQuery(id+"F0.wireOp",EDGE,"E46.MirrorCS"),sQuery(id+"F0.wireOp",EDGE,"E47.MirrorCS"),sQuery(id+"F0.wireOp",EDGE,"E48.MirrorCS"),sQuery(id+"F0.wireOp",EDGE,"E49.MirrorCS"),sQuery(id+"F0.wireOp",EDGE,"E50.MirrorCS"),sQuery(id+"F0.wireOp",EDGE,"E51.MirrorCS"),sQuery(id+"F0.wireOp",EDGE,"E52.MirrorCS"),sQuery(id+"F0.wireOp",EDGE,"E53.MirrorCS"),sQuery(id+"F0.wireOp",EDGE,"E54.MirrorCS"),sQuery(id+"F0.wireOp",EDGE,"E55.MirrorCS"),sQuery(id+"F0.wireOp",EDGE,"E56.MirrorCS"),sQuery(id+"F0.wireOp",EDGE,"E57.MirrorCS"),sQuery(id+"F0.wireOp",EDGE,"E58.MirrorCS"),sQuery(id+"F0.wireOp",EDGE,"E59.MirrorCS"),sQuery(id+"F0.wireOp",EDGE,"E60.MirrorCS"),sQuery(id+"F0.wireOp",EDGE,"E61.MirrorCS"),sQuery(id+"F0.wireOp",EDGE,"E62.MirrorCS"),sQuery(id+"F0.wireOp",EDGE,"E63.MirrorCS"),sQuery(id+"F0.wireOp",EDGE,"E64.MirrorCS"),sQuery(id+"F0.wireOp",EDGE,"E65.MirrorCS"),sQuery(id+"F0.wireOp",EDGE,"E66.MirrorCS"),sQuery(id+"F0.wireOp",EDGE,"E67.MirrorCS"),sQuery(id+"F0.wireOp",EDGE,"E68.trimOffspring"),sQuery(id+"F0.wireOp",EDGE,"E69.trimOffspring"),sQuery(id+"F0.wireOp",EDGE,"E70.trimOffspring"),sQuery(id+"F0.wireOp",EDGE,"E71.trimOffspring"),sQuery(id+"F0.wireOp",EDGE,"E72.trimOffspring"),sQuery(id+"F0.wireOp",EDGE,"E73.trimOffspring"),sQuery(id+"F0.wireOp",EDGE,"E74.trimOffspring"),sQuery(id+"F0.wireOp",EDGE,"E75.trimOffspring")])],"isStart":false});
            extrude(context, id + "F5", {"entities" : qUnion([Q0]), "operationType" : NewBodyOperationType.ADD, "endBound" : BoundingType.UP_TO_SURFACE, "oppositeDirection" : true, "endBoundEntityFace" : qUnion([Q1]), "depth" : 25 * mm});
        }
        {
            var Q0;
            {var subQ0=sQuery(id+"F0.wireOp",EDGE,"E75.trimOffspring");var subQ1=sQuery(id+"F0.wireOp",EDGE,"E74.trimOffspring");var subQ2=sQuery(id+"F0.wireOp",EDGE,"E73.trimOffspring");var subQ3=sQuery(id+"F0.wireOp",EDGE,"E72.trimOffspring");var subQ4=sQuery(id+"F0.wireOp",EDGE,"E71.trimOffspring");var subQ5=sQuery(id+"F0.wireOp",EDGE,"E70.trimOffspring");var subQ6=sQuery(id+"F0.wireOp",EDGE,"E69.trimOffspring");var subQ7=sQuery(id+"F0.wireOp",EDGE,"E68.trimOffspring");var subQ8=sQuery(id+"F0.wireOp",EDGE,"E67.MirrorCS");var subQ9=sQuery(id+"F0.wireOp",EDGE,"E66.MirrorCS");var subQ10=sQuery(id+"F0.wireOp",EDGE,"E65.MirrorCS");var subQ11=sQuery(id+"F0.wireOp",EDGE,"E64.MirrorCS");var subQ12=sQuery(id+"F0.wireOp",EDGE,"E63.MirrorCS");var subQ13=sQuery(id+"F0.wireOp",EDGE,"E62.MirrorCS");var subQ14=sQuery(id+"F0.wireOp",EDGE,"E61.MirrorCS");var subQ15=sQuery(id+"F0.wireOp",EDGE,"E60.MirrorCS");var subQ16=sQuery(id+"F0.wireOp",EDGE,"E59.MirrorCS");var subQ17=sQuery(id+"F0.wireOp",EDGE,"E58.MirrorCS");var subQ18=sQuery(id+"F0.wireOp",EDGE,"E57.MirrorCS");var subQ19=sQuery(id+"F0.wireOp",EDGE,"E56.MirrorCS");var subQ20=sQuery(id+"F0.wireOp",EDGE,"E55.MirrorCS");var subQ21=sQuery(id+"F0.wireOp",EDGE,"E54.MirrorCS");var subQ22=sQuery(id+"F0.wireOp",EDGE,"E53.MirrorCS");var subQ23=sQuery(id+"F0.wireOp",EDGE,"E52.MirrorCS");var subQ24=sQuery(id+"F0.wireOp",EDGE,"E51.MirrorCS");var subQ25=sQuery(id+"F0.wireOp",EDGE,"E50.MirrorCS");var subQ26=sQuery(id+"F0.wireOp",EDGE,"E49.MirrorCS");var subQ27=sQuery(id+"F0.wireOp",EDGE,"E48.MirrorCS");var subQ28=sQuery(id+"F0.wireOp",EDGE,"E47.MirrorCS");var subQ29=sQuery(id+"F0.wireOp",EDGE,"E46.MirrorCS");var subQ30=sQuery(id+"F0.wireOp",EDGE,"E45.MirrorCS");var subQ31=sQuery(id+"F0.wireOp",EDGE,"E44.MirrorCS");var subQ32=sQuery(id+"F0.wireOp",EDGE,"E43.MirrorCS");var subQ33=sQuery(id+"F0.wireOp",EDGE,"E42.MirrorCS");var subQ34=sQuery(id+"F0.wireOp",EDGE,"E41.MirrorCS");var subQ35=sQuery(id+"F0.wireOp",EDGE,"E40.MirrorCS");var subQ36=sQuery(id+"F0.wireOp",EDGE,"E38.MirrorCS");var subQ37=sQuery(id+"F0.wireOp",EDGE,"E37.MirrorCS");var subQ38=sQuery(id+"F0.wireOp",EDGE,"E36.MirrorCS");var subQ39=sQuery(id+"F0.wireOp",EDGE,"E35.MirrorCS");var subQ40=sQuery(id+"F0.wireOp",EDGE,"E34.MirrorCS");var subQ41=sQuery(id+"F0.wireOp",EDGE,"E33.MirrorCS");var subQ42=sQuery(id+"F0.wireOp",EDGE,"E32.MirrorCS");var subQ43=sQuery(id+"F0.wireOp",EDGE,"E31.MirrorCS");var subQ44=sQuery(id+"F0.wireOp",EDGE,"E30.MirrorCS");var subQ45=sQuery(id+"F0.wireOp",EDGE,"E29.MirrorCS");var subQ46=sQuery(id+"F0.wireOp",EDGE,"E28.MirrorCS");var subQ47=sQuery(id+"F0.wireOp",EDGE,"E27.MirrorCS");var subQ48=sQuery(id+"F0.wireOp",EDGE,"E26.MirrorCS");var subQ49=sQuery(id+"F0.wireOp",EDGE,"E25.MirrorCS");var subQ50=sQuery(id+"F0.wireOp",EDGE,"E24.MirrorCS");var subQ51=sQuery(id+"F0.wireOp",EDGE,"E23.MirrorCS");var subQ52=sQuery(id+"F0.wireOp",EDGE,"E22.MirrorCS");var subQ53=sQuery(id+"F0.wireOp",EDGE,"E21.MirrorCS");var subQ54=sQuery(id+"F0.wireOp",EDGE,"E20.MirrorCS");var subQ55=sQuery(id+"F0.wireOp",EDGE,"E19.MirrorCS");var subQ56=sQuery(id+"F0.wireOp",EDGE,"E18.MirrorCS");var subQ57=sQuery(id+"F0.wireOp",EDGE,"E17");var subQ58=sQuery(id+"F0.wireOp",EDGE,"E16");var subQ59=sQuery(id+"F0.wireOp",EDGE,"E15");var subQ60=sQuery(id+"F0.wireOp",EDGE,"E14");var subQ61=sQuery(id+"F0.wireOp",EDGE,"E13");var subQ62=sQuery(id+"F0.wireOp",EDGE,"E12");var subQ63=sQuery(id+"F0.wireOp",EDGE,"E11");var subQ64=sQuery(id+"F0.wireOp",EDGE,"E10.MirrorCS");var subQ65=sQuery(id+"F0.wireOp",EDGE,"E9.MirrorCS");var subQ66=sQuery(id+"F0.wireOp",EDGE,"E8.MirrorCS");var subQ67=sQuery(id+"F0.wireOp",EDGE,"E7.MirrorCS");var subQ68=sQuery(id+"F0.wireOp",EDGE,"E6.MirrorCS");var subQ69=sQuery(id+"F0.wireOp",EDGE,"E5.MirrorCS");var subQ70=sQuery(id+"F0.wireOp",EDGE,"E4");var subQ71=sQuery(id+"F0.wireOp",EDGE,"E3");var subQ72=sQuery(id+"F0.wireOp",EDGE,"E2.right");var subQ73=sQuery(id+"F0.wireOp",EDGE,"E2.left");var subQ74=sQuery(id+"F0.wireOp",EDGE,"E2.top");var subQ75=sQuery(id+"F0.wireOp",EDGE,"E2.bottom");Q0=makeQuery(id+"F5.boolean.opBoolean","MERGE",FACE,{"derivedFrom":[makeQuery(id+"F1.opExtrude","CAP_FACE",FACE,{"disambiguationData":[OSD([subQ75,subQ74,subQ73,subQ72,subQ71,subQ70,subQ69,subQ68,subQ67,subQ66,subQ65,subQ64,subQ63,subQ62,subQ61,subQ60,subQ59,subQ58,subQ57,subQ56,subQ55,subQ54,subQ53,subQ52,subQ51,subQ50,subQ49,subQ48,subQ47,subQ46,subQ45,subQ44,subQ43,subQ42,subQ41,subQ40,subQ39,subQ38,subQ37,subQ36,subQ35,subQ34,subQ33,subQ32,subQ31,subQ30,subQ29,subQ28,subQ27,subQ26,subQ25,subQ24,subQ23,subQ22,subQ21,subQ20,subQ19,subQ18,subQ17,subQ16,subQ15,subQ14,subQ13,subQ12,subQ11,subQ10,subQ9,subQ8,subQ7,subQ6,subQ5,subQ4,subQ3,subQ2,subQ1,subQ0])],"isStart":false}),makeQuery(id+"F5.opExtrude","CAP_FACE",FACE,{"disambiguationData":[OSD([subQ75,subQ74,subQ73,subQ72,subQ71,subQ70,subQ69,subQ68,subQ67,subQ66,subQ65,subQ64,subQ63,subQ62,subQ61,subQ60,subQ59,subQ58,subQ57,subQ56,subQ55,subQ54,subQ53,subQ52,subQ51,subQ50,subQ49,subQ48,subQ47,subQ46,subQ45,subQ44,subQ43,subQ42,subQ41,subQ40,subQ39,subQ38,subQ37,subQ36,subQ35,subQ34,subQ33,subQ32,subQ31,subQ30,subQ29,subQ28,subQ27,subQ26,subQ25,subQ24,subQ23,subQ22,subQ21,subQ20,subQ19,subQ18,subQ17,subQ16,subQ15,subQ14,subQ13,subQ12,subQ11,subQ10,subQ9,subQ8,subQ7,subQ6,subQ5,subQ4,subQ3,subQ2,subQ1,subQ0]),OD(0.0)],"isStart":false}),makeQuery(id+"F5.opExtrude","CAP_FACE",FACE,{"disambiguationData":[OSD([subQ75,subQ74,subQ73,subQ72,subQ71,subQ70,subQ69,subQ68,subQ67,subQ66,subQ65,subQ64,subQ63,subQ62,subQ61,subQ60,subQ59,subQ58,subQ57,subQ56,subQ55,subQ54,subQ53,subQ52,subQ51,subQ50,subQ49,subQ48,subQ47,subQ46,subQ45,subQ44,subQ43,subQ42,subQ41,subQ40,subQ39,subQ38,subQ37,subQ36,subQ35,subQ34,subQ33,subQ32,subQ31,subQ30,subQ29,subQ28,subQ27,subQ26,subQ25,subQ24,subQ23,subQ22,subQ21,subQ20,subQ19,subQ18,subQ17,subQ16,subQ15,subQ14,subQ13,subQ12,subQ11,subQ10,subQ9,subQ8,subQ7,subQ6,subQ5,subQ4,subQ3,subQ2,subQ1,subQ0]),OD(1.0)],"isStart":false}),makeQuery(id+"F5.opExtrude","CAP_FACE",FACE,{"disambiguationData":[OSD([subQ75,subQ74,subQ73,subQ72,subQ71,subQ70,subQ69,subQ68,subQ67,subQ66,subQ65,subQ64,subQ63,subQ62,subQ61,subQ60,subQ59,subQ58,subQ57,subQ56,subQ55,subQ54,subQ53,subQ52,subQ51,subQ50,subQ49,subQ48,subQ47,subQ46,subQ45,subQ44,subQ43,subQ42,subQ41,subQ40,subQ39,subQ38,subQ37,subQ36,subQ35,subQ34,subQ33,subQ32,subQ31,subQ30,subQ29,subQ28,subQ27,subQ26,subQ25,subQ24,subQ23,subQ22,subQ21,subQ20,subQ19,subQ18,subQ17,subQ16,subQ15,subQ14,subQ13,subQ12,subQ11,subQ10,subQ9,subQ8,subQ7,subQ6,subQ5,subQ4,subQ3,subQ2,subQ1,subQ0]),OD(2.0)],"isStart":false}),makeQuery(id+"F5.opExtrude","CAP_FACE",FACE,{"disambiguationData":[OSD([subQ75,subQ74,subQ73,subQ72,subQ71,subQ70,subQ69,subQ68,subQ67,subQ66,subQ65,subQ64,subQ63,subQ62,subQ61,subQ60,subQ59,subQ58,subQ57,subQ56,subQ55,subQ54,subQ53,subQ52,subQ51,subQ50,subQ49,subQ48,subQ47,subQ46,subQ45,subQ44,subQ43,subQ42,subQ41,subQ40,subQ39,subQ38,subQ37,subQ36,subQ35,subQ34,subQ33,subQ32,subQ31,subQ30,subQ29,subQ28,subQ27,subQ26,subQ25,subQ24,subQ23,subQ22,subQ21,subQ20,subQ19,subQ18,subQ17,subQ16,subQ15,subQ14,subQ13,subQ12,subQ11,subQ10,subQ9,subQ8,subQ7,subQ6,subQ5,subQ4,subQ3,subQ2,subQ1,subQ0]),OD(3.0)],"isStart":false}),makeQuery(id+"F5.opExtrude","CAP_FACE",FACE,{"disambiguationData":[OSD([subQ75,subQ74,subQ73,subQ72,subQ71,subQ70,subQ69,subQ68,subQ67,subQ66,subQ65,subQ64,subQ63,subQ62,subQ61,subQ60,subQ59,subQ58,subQ57,subQ56,subQ55,subQ54,subQ53,subQ52,subQ51,subQ50,subQ49,subQ48,subQ47,subQ46,subQ45,subQ44,subQ43,subQ42,subQ41,subQ40,subQ39,subQ38,subQ37,subQ36,subQ35,subQ34,subQ33,subQ32,subQ31,subQ30,subQ29,subQ28,subQ27,subQ26,subQ25,subQ24,subQ23,subQ22,subQ21,subQ20,subQ19,subQ18,subQ17,subQ16,subQ15,subQ14,subQ13,subQ12,subQ11,subQ10,subQ9,subQ8,subQ7,subQ6,subQ5,subQ4,subQ3,subQ2,subQ1,subQ0]),OD(4.0)],"isStart":false}),makeQuery(id+"F5.opExtrude","CAP_FACE",FACE,{"disambiguationData":[OSD([subQ75,subQ74,subQ73,subQ72,subQ71,subQ70,subQ69,subQ68,subQ67,subQ66,subQ65,subQ64,subQ63,subQ62,subQ61,subQ60,subQ59,subQ58,subQ57,subQ56,subQ55,subQ54,subQ53,subQ52,subQ51,subQ50,subQ49,subQ48,subQ47,subQ46,subQ45,subQ44,subQ43,subQ42,subQ41,subQ40,subQ39,subQ38,subQ37,subQ36,subQ35,subQ34,subQ33,subQ32,subQ31,subQ30,subQ29,subQ28,subQ27,subQ26,subQ25,subQ24,subQ23,subQ22,subQ21,subQ20,subQ19,subQ18,subQ17,subQ16,subQ15,subQ14,subQ13,subQ12,subQ11,subQ10,subQ9,subQ8,subQ7,subQ6,subQ5,subQ4,subQ3,subQ2,subQ1,subQ0]),OD(5.0)],"isStart":false}),makeQuery(id+"F5.opExtrude","CAP_FACE",FACE,{"disambiguationData":[OSD([subQ75,subQ74,subQ73,subQ72,subQ71,subQ70,subQ69,subQ68,subQ67,subQ66,subQ65,subQ64,subQ63,subQ62,subQ61,subQ60,subQ59,subQ58,subQ57,subQ56,subQ55,subQ54,subQ53,subQ52,subQ51,subQ50,subQ49,subQ48,subQ47,subQ46,subQ45,subQ44,subQ43,subQ42,subQ41,subQ40,subQ39,subQ38,subQ37,subQ36,subQ35,subQ34,subQ33,subQ32,subQ31,subQ30,subQ29,subQ28,subQ27,subQ26,subQ25,subQ24,subQ23,subQ22,subQ21,subQ20,subQ19,subQ18,subQ17,subQ16,subQ15,subQ14,subQ13,subQ12,subQ11,subQ10,subQ9,subQ8,subQ7,subQ6,subQ5,subQ4,subQ3,subQ2,subQ1,subQ0]),OD(6.0)],"isStart":false}),makeQuery(id+"F5.opExtrude","CAP_FACE",FACE,{"disambiguationData":[OSD([subQ75,subQ74,subQ73,subQ72,subQ71,subQ70,subQ69,subQ68,subQ67,subQ66,subQ65,subQ64,subQ63,subQ62,subQ61,subQ60,subQ59,subQ58,subQ57,subQ56,subQ55,subQ54,subQ53,subQ52,subQ51,subQ50,subQ49,subQ48,subQ47,subQ46,subQ45,subQ44,subQ43,subQ42,subQ41,subQ40,subQ39,subQ38,subQ37,subQ36,subQ35,subQ34,subQ33,subQ32,subQ31,subQ30,subQ29,subQ28,subQ27,subQ26,subQ25,subQ24,subQ23,subQ22,subQ21,subQ20,subQ19,subQ18,subQ17,subQ16,subQ15,subQ14,subQ13,subQ12,subQ11,subQ10,subQ9,subQ8,subQ7,subQ6,subQ5,subQ4,subQ3,subQ2,subQ1,subQ0]),OD(7.0)],"isStart":false}),makeQuery(id+"F5.opExtrude","CAP_FACE",FACE,{"disambiguationData":[OSD([subQ75,subQ74,subQ73,subQ72,subQ71,subQ70,subQ69,subQ68,subQ67,subQ66,subQ65,subQ64,subQ63,subQ62,subQ61,subQ60,subQ59,subQ58,subQ57,subQ56,subQ55,subQ54,subQ53,subQ52,subQ51,subQ50,subQ49,subQ48,subQ47,subQ46,subQ45,subQ44,subQ43,subQ42,subQ41,subQ40,subQ39,subQ38,subQ37,subQ36,subQ35,subQ34,subQ33,subQ32,subQ31,subQ30,subQ29,subQ28,subQ27,subQ26,subQ25,subQ24,subQ23,subQ22,subQ21,subQ20,subQ19,subQ18,subQ17,subQ16,subQ15,subQ14,subQ13,subQ12,subQ11,subQ10,subQ9,subQ8,subQ7,subQ6,subQ5,subQ4,subQ3,subQ2,subQ1,subQ0]),OD(8.0)],"isStart":false}),makeQuery(id+"F5.opExtrude","CAP_FACE",FACE,{"disambiguationData":[OSD([subQ75,subQ74,subQ73,subQ72,subQ71,subQ70,subQ69,subQ68,subQ67,subQ66,subQ65,subQ64,subQ63,subQ62,subQ61,subQ60,subQ59,subQ58,subQ57,subQ56,subQ55,subQ54,subQ53,subQ52,subQ51,subQ50,subQ49,subQ48,subQ47,subQ46,subQ45,subQ44,subQ43,subQ42,subQ41,subQ40,subQ39,subQ38,subQ37,subQ36,subQ35,subQ34,subQ33,subQ32,subQ31,subQ30,subQ29,subQ28,subQ27,subQ26,subQ25,subQ24,subQ23,subQ22,subQ21,subQ20,subQ19,subQ18,subQ17,subQ16,subQ15,subQ14,subQ13,subQ12,subQ11,subQ10,subQ9,subQ8,subQ7,subQ6,subQ5,subQ4,subQ3,subQ2,subQ1,subQ0]),OD(9.0)],"isStart":false}),makeQuery(id+"F5.opExtrude","CAP_FACE",FACE,{"disambiguationData":[OSD([subQ75,subQ74,subQ73,subQ72,subQ71,subQ70,subQ69,subQ68,subQ67,subQ66,subQ65,subQ64,subQ63,subQ62,subQ61,subQ60,subQ59,subQ58,subQ57,subQ56,subQ55,subQ54,subQ53,subQ52,subQ51,subQ50,subQ49,subQ48,subQ47,subQ46,subQ45,subQ44,subQ43,subQ42,subQ41,subQ40,subQ39,subQ38,subQ37,subQ36,subQ35,subQ34,subQ33,subQ32,subQ31,subQ30,subQ29,subQ28,subQ27,subQ26,subQ25,subQ24,subQ23,subQ22,subQ21,subQ20,subQ19,subQ18,subQ17,subQ16,subQ15,subQ14,subQ13,subQ12,subQ11,subQ10,subQ9,subQ8,subQ7,subQ6,subQ5,subQ4,subQ3,subQ2,subQ1,subQ0]),OD(10.0)],"isStart":false}),makeQuery(id+"F5.opExtrude","CAP_FACE",FACE,{"disambiguationData":[OSD([subQ75,subQ74,subQ73,subQ72,subQ71,subQ70,subQ69,subQ68,subQ67,subQ66,subQ65,subQ64,subQ63,subQ62,subQ61,subQ60,subQ59,subQ58,subQ57,subQ56,subQ55,subQ54,subQ53,subQ52,subQ51,subQ50,subQ49,subQ48,subQ47,subQ46,subQ45,subQ44,subQ43,subQ42,subQ41,subQ40,subQ39,subQ38,subQ37,subQ36,subQ35,subQ34,subQ33,subQ32,subQ31,subQ30,subQ29,subQ28,subQ27,subQ26,subQ25,subQ24,subQ23,subQ22,subQ21,subQ20,subQ19,subQ18,subQ17,subQ16,subQ15,subQ14,subQ13,subQ12,subQ11,subQ10,subQ9,subQ8,subQ7,subQ6,subQ5,subQ4,subQ3,subQ2,subQ1,subQ0]),OD(11.0)],"isStart":false}),makeQuery(id+"F5.opExtrude","CAP_FACE",FACE,{"disambiguationData":[OSD([subQ75,subQ74,subQ73,subQ72,subQ71,subQ70,subQ69,subQ68,subQ67,subQ66,subQ65,subQ64,subQ63,subQ62,subQ61,subQ60,subQ59,subQ58,subQ57,subQ56,subQ55,subQ54,subQ53,subQ52,subQ51,subQ50,subQ49,subQ48,subQ47,subQ46,subQ45,subQ44,subQ43,subQ42,subQ41,subQ40,subQ39,subQ38,subQ37,subQ36,subQ35,subQ34,subQ33,subQ32,subQ31,subQ30,subQ29,subQ28,subQ27,subQ26,subQ25,subQ24,subQ23,subQ22,subQ21,subQ20,subQ19,subQ18,subQ17,subQ16,subQ15,subQ14,subQ13,subQ12,subQ11,subQ10,subQ9,subQ8,subQ7,subQ6,subQ5,subQ4,subQ3,subQ2,subQ1,subQ0]),OD(12.0)],"isStart":false}),makeQuery(id+"F5.opExtrude","CAP_FACE",FACE,{"disambiguationData":[OSD([subQ75,subQ74,subQ73,subQ72,subQ71,subQ70,subQ69,subQ68,subQ67,subQ66,subQ65,subQ64,subQ63,subQ62,subQ61,subQ60,subQ59,subQ58,subQ57,subQ56,subQ55,subQ54,subQ53,subQ52,subQ51,subQ50,subQ49,subQ48,subQ47,subQ46,subQ45,subQ44,subQ43,subQ42,subQ41,subQ40,subQ39,subQ38,subQ37,subQ36,subQ35,subQ34,subQ33,subQ32,subQ31,subQ30,subQ29,subQ28,subQ27,subQ26,subQ25,subQ24,subQ23,subQ22,subQ21,subQ20,subQ19,subQ18,subQ17,subQ16,subQ15,subQ14,subQ13,subQ12,subQ11,subQ10,subQ9,subQ8,subQ7,subQ6,subQ5,subQ4,subQ3,subQ2,subQ1,subQ0]),OD(13.0)],"isStart":false}),makeQuery(id+"F5.opExtrude","CAP_FACE",FACE,{"disambiguationData":[OSD([subQ75,subQ74,subQ73,subQ72,subQ71,subQ70,subQ69,subQ68,subQ67,subQ66,subQ65,subQ64,subQ63,subQ62,subQ61,subQ60,subQ59,subQ58,subQ57,subQ56,subQ55,subQ54,subQ53,subQ52,subQ51,subQ50,subQ49,subQ48,subQ47,subQ46,subQ45,subQ44,subQ43,subQ42,subQ41,subQ40,subQ39,subQ38,subQ37,subQ36,subQ35,subQ34,subQ33,subQ32,subQ31,subQ30,subQ29,subQ28,subQ27,subQ26,subQ25,subQ24,subQ23,subQ22,subQ21,subQ20,subQ19,subQ18,subQ17,subQ16,subQ15,subQ14,subQ13,subQ12,subQ11,subQ10,subQ9,subQ8,subQ7,subQ6,subQ5,subQ4,subQ3,subQ2,subQ1,subQ0]),OD(14.0)],"isStart":false}),makeQuery(id+"F5.opExtrude","CAP_FACE",FACE,{"disambiguationData":[OSD([subQ75,subQ74,subQ73,subQ72,subQ71,subQ70,subQ69,subQ68,subQ67,subQ66,subQ65,subQ64,subQ63,subQ62,subQ61,subQ60,subQ59,subQ58,subQ57,subQ56,subQ55,subQ54,subQ53,subQ52,subQ51,subQ50,subQ49,subQ48,subQ47,subQ46,subQ45,subQ44,subQ43,subQ42,subQ41,subQ40,subQ39,subQ38,subQ37,subQ36,subQ35,subQ34,subQ33,subQ32,subQ31,subQ30,subQ29,subQ28,subQ27,subQ26,subQ25,subQ24,subQ23,subQ22,subQ21,subQ20,subQ19,subQ18,subQ17,subQ16,subQ15,subQ14,subQ13,subQ12,subQ11,subQ10,subQ9,subQ8,subQ7,subQ6,subQ5,subQ4,subQ3,subQ2,subQ1,subQ0]),OD(15.0)],"isStart":false}),makeQuery(id+"F5.opExtrude","CAP_FACE",FACE,{"disambiguationData":[OSD([subQ75,subQ74,subQ73,subQ72,subQ71,subQ70,subQ69,subQ68,subQ67,subQ66,subQ65,subQ64,subQ63,subQ62,subQ61,subQ60,subQ59,subQ58,subQ57,subQ56,subQ55,subQ54,subQ53,subQ52,subQ51,subQ50,subQ49,subQ48,subQ47,subQ46,subQ45,subQ44,subQ43,subQ42,subQ41,subQ40,subQ39,subQ38,subQ37,subQ36,subQ35,subQ34,subQ33,subQ32,subQ31,subQ30,subQ29,subQ28,subQ27,subQ26,subQ25,subQ24,subQ23,subQ22,subQ21,subQ20,subQ19,subQ18,subQ17,subQ16,subQ15,subQ14,subQ13,subQ12,subQ11,subQ10,subQ9,subQ8,subQ7,subQ6,subQ5,subQ4,subQ3,subQ2,subQ1,subQ0]),OD(16.0)],"isStart":false}),makeQuery(id+"F5.opExtrude","CAP_FACE",FACE,{"disambiguationData":[OSD([subQ75,subQ74,subQ73,subQ72,subQ71,subQ70,subQ69,subQ68,subQ67,subQ66,subQ65,subQ64,subQ63,subQ62,subQ61,subQ60,subQ59,subQ58,subQ57,subQ56,subQ55,subQ54,subQ53,subQ52,subQ51,subQ50,subQ49,subQ48,subQ47,subQ46,subQ45,subQ44,subQ43,subQ42,subQ41,subQ40,subQ39,subQ38,subQ37,subQ36,subQ35,subQ34,subQ33,subQ32,subQ31,subQ30,subQ29,subQ28,subQ27,subQ26,subQ25,subQ24,subQ23,subQ22,subQ21,subQ20,subQ19,subQ18,subQ17,subQ16,subQ15,subQ14,subQ13,subQ12,subQ11,subQ10,subQ9,subQ8,subQ7,subQ6,subQ5,subQ4,subQ3,subQ2,subQ1,subQ0]),OD(17.0)],"isStart":false}),makeQuery(id+"F5.opExtrude","CAP_FACE",FACE,{"disambiguationData":[OSD([subQ75,subQ74,subQ73,subQ72,subQ71,subQ70,subQ69,subQ68,subQ67,subQ66,subQ65,subQ64,subQ63,subQ62,subQ61,subQ60,subQ59,subQ58,subQ57,subQ56,subQ55,subQ54,subQ53,subQ52,subQ51,subQ50,subQ49,subQ48,subQ47,subQ46,subQ45,subQ44,subQ43,subQ42,subQ41,subQ40,subQ39,subQ38,subQ37,subQ36,subQ35,subQ34,subQ33,subQ32,subQ31,subQ30,subQ29,subQ28,subQ27,subQ26,subQ25,subQ24,subQ23,subQ22,subQ21,subQ20,subQ19,subQ18,subQ17,subQ16,subQ15,subQ14,subQ13,subQ12,subQ11,subQ10,subQ9,subQ8,subQ7,subQ6,subQ5,subQ4,subQ3,subQ2,subQ1,subQ0]),OD(18.0)],"isStart":false}),makeQuery(id+"F5.opExtrude","CAP_FACE",FACE,{"disambiguationData":[OSD([subQ75,subQ74,subQ73,subQ72,subQ71,subQ70,subQ69,subQ68,subQ67,subQ66,subQ65,subQ64,subQ63,subQ62,subQ61,subQ60,subQ59,subQ58,subQ57,subQ56,subQ55,subQ54,subQ53,subQ52,subQ51,subQ50,subQ49,subQ48,subQ47,subQ46,subQ45,subQ44,subQ43,subQ42,subQ41,subQ40,subQ39,subQ38,subQ37,subQ36,subQ35,subQ34,subQ33,subQ32,subQ31,subQ30,subQ29,subQ28,subQ27,subQ26,subQ25,subQ24,subQ23,subQ22,subQ21,subQ20,subQ19,subQ18,subQ17,subQ16,subQ15,subQ14,subQ13,subQ12,subQ11,subQ10,subQ9,subQ8,subQ7,subQ6,subQ5,subQ4,subQ3,subQ2,subQ1,subQ0]),OD(19.0)],"isStart":false})]});}
            var sketch = newSketch(context, id + "F6", { "sketchPlane" : qUnion([Q0])});
            skArc(sketch, "E165.0", {"start": v(-45.65, 43.53) * mm, "mid": v(-47.64, 44.11) * mm, "end": v(-48.5, 46) * mm, "construction": true});
            skCircle(sketch, "E166", {"center": v(-46, 46) * mm, "radius": 2.5 * mm});
            skCircle(sketch, "E167", {"center": v(46, 46) * mm, "radius": 2.5 * mm});
            skCircle(sketch, "E168", {"center": v(-46, -46) * mm, "radius": 2.5 * mm});
            skCircle(sketch, "E169", {"center": v(46, -46) * mm, "radius": 2.5 * mm});
            skSolve(sketch);
        }
        {
            var Q0;
            Q0=qSketchRegion(id+"F6",true);
            extrude(context, id + "F7", {"entities" : qUnion([Q0]), "operationType" : NewBodyOperationType.REMOVE, "endBound" : BoundingType.THROUGH_ALL, "oppositeDirection" : true, "depth" : 25 * mm, "offsetDistance" : 25 * mm});
        }
        {
            var Q0;
            Q0=makeQuery(id+"F1.opExtrude","SWEPT_EDGE",EDGE,{"disambiguationData":[OSD([sQuery(id+"F0.wireOp",EDGE,"E6.MirrorCS"),sQuery(id+"F0.wireOp",EDGE,"E71.trimOffspring")])]});
            var Q1;
            Q1=makeQuery(id+"F1.opExtrude","SWEPT_EDGE",EDGE,{"disambiguationData":[OSD([sQuery(id+"F0.wireOp",EDGE,"E7.MirrorCS"),sQuery(id+"F0.wireOp",EDGE,"E72.trimOffspring")])]});
            var Q2;
            Q2=makeQuery(id+"F1.opExtrude","SWEPT_EDGE",EDGE,{"disambiguationData":[OSD([sQuery(id+"F0.wireOp",EDGE,"E9.MirrorCS"),sQuery(id+"F0.wireOp",EDGE,"E75.trimOffspring")])]});
            var Q3;
            Q3=makeQuery(id+"F1.opExtrude","SWEPT_EDGE",EDGE,{"disambiguationData":[OSD([sQuery(id+"F0.wireOp",EDGE,"E4"),sQuery(id+"F0.wireOp",EDGE,"E68.trimOffspring")])]});
            fillet(context, id + "F8", {"entities" : qUnion([Q0, Q1, Q2, Q3]), "radius" : 3 * mm, "tangentPropagation" : true, "allowEdgeOverflow" : false});
        }
        {
            var Q0;
            Q0=makeQuery(id+"F1.opExtrude","SWEPT_EDGE",EDGE,{"disambiguationData":[OSD([sQuery(id+"F0.wireOp",EDGE,"E13"),sQuery(id+"F0.wireOp",EDGE,"E14")])]});
            var Q1;
            Q1=makeQuery(id+"F1.opExtrude","SWEPT_EDGE",EDGE,{"disambiguationData":[OSD([sQuery(id+"F0.wireOp",EDGE,"E12"),sQuery(id+"F0.wireOp",EDGE,"E13")])]});
            var Q2;
            Q2=makeQuery(id+"F1.opExtrude","SWEPT_EDGE",EDGE,{"disambiguationData":[OSD([sQuery(id+"F0.wireOp",EDGE,"E14"),sQuery(id+"F0.wireOp",EDGE,"E15")])]});
            var Q3;
            Q3=makeQuery(id+"F1.opExtrude","SWEPT_EDGE",EDGE,{"disambiguationData":[OSD([sQuery(id+"F0.wireOp",EDGE,"E15"),sQuery(id+"F0.wireOp",EDGE,"E16")])]});
            var Q4;
            Q4=makeQuery(id+"F1.opExtrude","SWEPT_EDGE",EDGE,{"disambiguationData":[OSD([sQuery(id+"F0.wireOp",EDGE,"E58.MirrorCS"),sQuery(id+"F0.wireOp",EDGE,"E62.MirrorCS")])]});
            var Q5;
            Q5=makeQuery(id+"F1.opExtrude","SWEPT_EDGE",EDGE,{"disambiguationData":[OSD([sQuery(id+"F0.wireOp",EDGE,"E56.MirrorCS"),sQuery(id+"F0.wireOp",EDGE,"E58.MirrorCS")])]});
            var Q6;
            Q6=makeQuery(id+"F1.opExtrude","SWEPT_EDGE",EDGE,{"disambiguationData":[OSD([sQuery(id+"F0.wireOp",EDGE,"E54.MirrorCS"),sQuery(id+"F0.wireOp",EDGE,"E56.MirrorCS")])]});
            var Q7;
            Q7=makeQuery(id+"F1.opExtrude","SWEPT_EDGE",EDGE,{"disambiguationData":[OSD([sQuery(id+"F0.wireOp",EDGE,"E54.MirrorCS"),sQuery(id+"F0.wireOp",EDGE,"E57.MirrorCS")])]});
            var Q8;
            Q8=makeQuery(id+"F1.opExtrude","SWEPT_EDGE",EDGE,{"disambiguationData":[OSD([sQuery(id+"F0.wireOp",EDGE,"E59.MirrorCS"),sQuery(id+"F0.wireOp",EDGE,"E67.MirrorCS")])]});
            var Q9;
            Q9=makeQuery(id+"F1.opExtrude","SWEPT_EDGE",EDGE,{"disambiguationData":[OSD([sQuery(id+"F0.wireOp",EDGE,"E66.MirrorCS"),sQuery(id+"F0.wireOp",EDGE,"E67.MirrorCS")])]});
            var Q10;
            Q10=makeQuery(id+"F1.opExtrude","SWEPT_EDGE",EDGE,{"disambiguationData":[OSD([sQuery(id+"F0.wireOp",EDGE,"E59.MirrorCS"),sQuery(id+"F0.wireOp",EDGE,"E64.MirrorCS")])]});
            var Q11;
            Q11=makeQuery(id+"F1.opExtrude","SWEPT_EDGE",EDGE,{"disambiguationData":[OSD([sQuery(id+"F0.wireOp",EDGE,"E64.MirrorCS"),sQuery(id+"F0.wireOp",EDGE,"E65.MirrorCS")])]});
            var Q12;
            Q12=makeQuery(id+"F1.opExtrude","SWEPT_EDGE",EDGE,{"disambiguationData":[OSD([sQuery(id+"F0.wireOp",EDGE,"E25.MirrorCS"),sQuery(id+"F0.wireOp",EDGE,"E28.MirrorCS")])]});
            var Q13;
            Q13=makeQuery(id+"F1.opExtrude","SWEPT_EDGE",EDGE,{"disambiguationData":[OSD([sQuery(id+"F0.wireOp",EDGE,"E25.MirrorCS"),sQuery(id+"F0.wireOp",EDGE,"E37.MirrorCS")])]});
            var Q14;
            Q14=makeQuery(id+"F1.opExtrude","SWEPT_EDGE",EDGE,{"disambiguationData":[OSD([sQuery(id+"F0.wireOp",EDGE,"E28.MirrorCS"),sQuery(id+"F0.wireOp",EDGE,"E31.MirrorCS")])]});
            var Q15;
            Q15=makeQuery(id+"F1.opExtrude","SWEPT_EDGE",EDGE,{"disambiguationData":[OSD([sQuery(id+"F0.wireOp",EDGE,"E31.MirrorCS"),sQuery(id+"F0.wireOp",EDGE,"E38.MirrorCS")])]});
            var Q16;
            Q16=makeQuery(id+"F1.opExtrude","SWEPT_EDGE",EDGE,{"disambiguationData":[OSD([sQuery(id+"F0.wireOp",EDGE,"E27.MirrorCS"),sQuery(id+"F0.wireOp",EDGE,"E30.MirrorCS")])]});
            var Q17;
            Q17=makeQuery(id+"F1.opExtrude","SWEPT_EDGE",EDGE,{"disambiguationData":[OSD([sQuery(id+"F0.wireOp",EDGE,"E26.MirrorCS"),sQuery(id+"F0.wireOp",EDGE,"E30.MirrorCS")])]});
            var Q18;
            Q18=makeQuery(id+"F1.opExtrude","SWEPT_EDGE",EDGE,{"disambiguationData":[OSD([sQuery(id+"F0.wireOp",EDGE,"E26.MirrorCS"),sQuery(id+"F0.wireOp",EDGE,"E35.MirrorCS")])]});
            var Q19;
            Q19=makeQuery(id+"F1.opExtrude","SWEPT_EDGE",EDGE,{"disambiguationData":[OSD([sQuery(id+"F0.wireOp",EDGE,"E29.MirrorCS"),sQuery(id+"F0.wireOp",EDGE,"E35.MirrorCS")])]});
            var Q20;
            Q20=makeQuery(id+"F1.opExtrude","SWEPT_EDGE",EDGE,{"disambiguationData":[OSD([sQuery(id+"F0.wireOp",EDGE,"E48.MirrorCS"),sQuery(id+"F0.wireOp",EDGE,"E51.MirrorCS")])]});
            var Q21;
            Q21=makeQuery(id+"F1.opExtrude","SWEPT_EDGE",EDGE,{"disambiguationData":[OSD([sQuery(id+"F0.wireOp",EDGE,"E47.MirrorCS"),sQuery(id+"F0.wireOp",EDGE,"E51.MirrorCS")])]});
            var Q22;
            Q22=makeQuery(id+"F1.opExtrude","SWEPT_EDGE",EDGE,{"disambiguationData":[OSD([sQuery(id+"F0.wireOp",EDGE,"E48.MirrorCS"),sQuery(id+"F0.wireOp",EDGE,"E52.MirrorCS")])]});
            var Q23;
            Q23=makeQuery(id+"F1.opExtrude","SWEPT_EDGE",EDGE,{"disambiguationData":[OSD([sQuery(id+"F0.wireOp",EDGE,"E49.MirrorCS"),sQuery(id+"F0.wireOp",EDGE,"E52.MirrorCS")])]});
            var Q24;
            Q24=makeQuery(id+"F1.opExtrude","SWEPT_EDGE",EDGE,{"disambiguationData":[OSD([sQuery(id+"F0.wireOp",EDGE,"E43.MirrorCS"),sQuery(id+"F0.wireOp",EDGE,"E44.MirrorCS")])]});
            var Q25;
            Q25=makeQuery(id+"F1.opExtrude","SWEPT_EDGE",EDGE,{"disambiguationData":[OSD([sQuery(id+"F0.wireOp",EDGE,"E44.MirrorCS"),sQuery(id+"F0.wireOp",EDGE,"E46.MirrorCS")])]});
            var Q26;
            Q26=makeQuery(id+"F1.opExtrude","SWEPT_EDGE",EDGE,{"disambiguationData":[OSD([sQuery(id+"F0.wireOp",EDGE,"E40.MirrorCS"),sQuery(id+"F0.wireOp",EDGE,"E41.MirrorCS")])]});
            var Q27;
            Q27=makeQuery(id+"F1.opExtrude","SWEPT_EDGE",EDGE,{"disambiguationData":[OSD([sQuery(id+"F0.wireOp",EDGE,"E40.MirrorCS"),sQuery(id+"F0.wireOp",EDGE,"E43.MirrorCS")])]});
            var Q28;
            Q28=makeQuery(id+"F1.opExtrude","SWEPT_EDGE",EDGE,{"disambiguationData":[OSD([sQuery(id+"F0.wireOp",EDGE,"E19.MirrorCS"),sQuery(id+"F0.wireOp",EDGE,"E23.MirrorCS")])]});
            var Q29;
            Q29=makeQuery(id+"F1.opExtrude","SWEPT_EDGE",EDGE,{"disambiguationData":[OSD([sQuery(id+"F0.wireOp",EDGE,"E19.MirrorCS"),sQuery(id+"F0.wireOp",EDGE,"E21.MirrorCS")])]});
            var Q30;
            Q30=makeQuery(id+"F1.opExtrude","SWEPT_EDGE",EDGE,{"disambiguationData":[OSD([sQuery(id+"F0.wireOp",EDGE,"E21.MirrorCS"),sQuery(id+"F0.wireOp",EDGE,"E22.MirrorCS")])]});
            var Q31;
            Q31=makeQuery(id+"F1.opExtrude","SWEPT_EDGE",EDGE,{"disambiguationData":[OSD([sQuery(id+"F0.wireOp",EDGE,"E18.MirrorCS"),sQuery(id+"F0.wireOp",EDGE,"E23.MirrorCS")])]});
            fillet(context, id + "F9", {"entities" : qUnion([Q0, Q1, Q2, Q3, Q4, Q5, Q6, Q7, Q8, Q9, Q10, Q11, Q12, Q13, Q14, Q15, Q16, Q17, Q18, Q19, Q20, Q21, Q22, Q23, Q24, Q25, Q26, Q27, Q28, Q29, Q30, Q31]), "radius" : 1 * mm, "tangentPropagation" : true, "allowEdgeOverflow" : false});
        }
        {
            var Q0;
            Q0=makeQuery(id+"F5.boolean.opBoolean","INTERSECT",EDGE,{"derivedFrom":[makeQuery(id+"F2.opShell","OFFSET_FACE",FACE,{"disambiguationData":[OSD([sQuery(id+"F0.wireOp",EDGE,"E9.MirrorCS")])]}),makeQuery(id+"F5.opExtrude","SWEPT_FACE",FACE,{"disambiguationData":[OSD([sQuery(id+"F4.wireOp",EDGE,"E163.MirrorCS")])]})]});
            var Q1;
            Q1=makeQuery(id+"F5.boolean.opBoolean","INTERSECT",EDGE,{"derivedFrom":[makeQuery(id+"F2.opShell","OFFSET_FACE",FACE,{"disambiguationData":[OSD([sQuery(id+"F0.wireOp",EDGE,"E75.trimOffspring")])]}),makeQuery(id+"F5.opExtrude","SWEPT_FACE",FACE,{"disambiguationData":[OSD([sQuery(id+"F4.wireOp",EDGE,"E163.MirrorCS")])]})]});
            var Q2;
            Q2=makeQuery(id+"F5.boolean.opBoolean","INTERSECT",EDGE,{"derivedFrom":[makeQuery(id+"F2.opShell","OFFSET_FACE",FACE,{"disambiguationData":[OSD([sQuery(id+"F0.wireOp",EDGE,"E4")])]}),makeQuery(id+"F5.opExtrude","SWEPT_FACE",FACE,{"disambiguationData":[OSD([sQuery(id+"F4.wireOp",EDGE,"E142.0")])]})]});
            var Q3;
            Q3=makeQuery(id+"F5.boolean.opBoolean","INTERSECT",EDGE,{"derivedFrom":[makeQuery(id+"F2.opShell","OFFSET_FACE",FACE,{"disambiguationData":[OSD([sQuery(id+"F0.wireOp",EDGE,"E68.trimOffspring")])]}),makeQuery(id+"F5.opExtrude","SWEPT_FACE",FACE,{"disambiguationData":[OSD([sQuery(id+"F4.wireOp",EDGE,"E142.0")])]})]});
            var Q4;
            Q4=makeQuery(id+"F5.boolean.opBoolean","INTERSECT",EDGE,{"derivedFrom":[makeQuery(id+"F2.opShell","OFFSET_FACE",FACE,{"disambiguationData":[OSD([sQuery(id+"F0.wireOp",EDGE,"E71.trimOffspring")])]}),makeQuery(id+"F5.opExtrude","SWEPT_FACE",FACE,{"disambiguationData":[OSD([sQuery(id+"F4.wireOp",EDGE,"E149.MirrorCS")])]})]});
            var Q5;
            Q5=makeQuery(id+"F5.boolean.opBoolean","INTERSECT",EDGE,{"derivedFrom":[makeQuery(id+"F2.opShell","OFFSET_FACE",FACE,{"disambiguationData":[OSD([sQuery(id+"F0.wireOp",EDGE,"E6.MirrorCS")])]}),makeQuery(id+"F5.opExtrude","SWEPT_FACE",FACE,{"disambiguationData":[OSD([sQuery(id+"F4.wireOp",EDGE,"E149.MirrorCS")])]})]});
            var Q6;
            Q6=makeQuery(id+"F5.boolean.opBoolean","INTERSECT",EDGE,{"derivedFrom":[makeQuery(id+"F2.opShell","OFFSET_FACE",FACE,{"disambiguationData":[OSD([sQuery(id+"F0.wireOp",EDGE,"E7.MirrorCS")])]}),makeQuery(id+"F5.opExtrude","SWEPT_FACE",FACE,{"disambiguationData":[OSD([sQuery(id+"F4.wireOp",EDGE,"E161.MirrorCS")])]})]});
            var Q7;
            Q7=makeQuery(id+"F5.boolean.opBoolean","INTERSECT",EDGE,{"derivedFrom":[makeQuery(id+"F2.opShell","OFFSET_FACE",FACE,{"disambiguationData":[OSD([sQuery(id+"F0.wireOp",EDGE,"E72.trimOffspring")])]}),makeQuery(id+"F5.opExtrude","SWEPT_FACE",FACE,{"disambiguationData":[OSD([sQuery(id+"F4.wireOp",EDGE,"E161.MirrorCS")])]})]});
            fillet(context, id + "F10", {"entities" : qUnion([Q0, Q1, Q2, Q3, Q4, Q5, Q6, Q7]), "radius" : 2 * mm, "tangentPropagation" : true, "allowEdgeOverflow" : false});
        }
        {
            var Q0;
            Q0=makeQuery(id+"F5.opExtrude","SWEPT_EDGE",EDGE,{"disambiguationData":[OSD([sQuery(id+"F0.wireOp",EDGE,"E19.MirrorCS"),sQuery(id+"F4.wireOp",EDGE,"E105.MirrorCS"),sQuery(id+"F4.wireOp",EDGE,"E106.MirrorCS")])]});
            var Q1;
            Q1=makeQuery(id+"F5.opExtrude","SWEPT_EDGE",EDGE,{"disambiguationData":[OSD([sQuery(id+"F0.wireOp",EDGE,"E19.MirrorCS"),sQuery(id+"F4.wireOp",EDGE,"E100.MirrorCS"),sQuery(id+"F4.wireOp",EDGE,"E105.MirrorCS")])]});
            var Q2;
            Q2=makeQuery(id+"F5.opExtrude","SWEPT_EDGE",EDGE,{"disambiguationData":[OSD([sQuery(id+"F4.wireOp",EDGE,"E100.MirrorCS"),sQuery(id+"F4.wireOp",EDGE,"E101.MirrorCS")])]});
            var Q3;
            Q3=makeQuery(id+"F5.opExtrude","SWEPT_EDGE",EDGE,{"disambiguationData":[OSD([sQuery(id+"F4.wireOp",EDGE,"E101.MirrorCS"),sQuery(id+"F4.wireOp",EDGE,"E106.MirrorCS")])]});
            var Q4;
            Q4=makeQuery(id+"F5.opExtrude","SWEPT_EDGE",EDGE,{"disambiguationData":[OSD([sQuery(id+"F4.wireOp",EDGE,"E77"),sQuery(id+"F4.wireOp",EDGE,"E78")])]});
            var Q5;
            Q5=makeQuery(id+"F5.opExtrude","SWEPT_EDGE",EDGE,{"disambiguationData":[OSD([sQuery(id+"F0.wireOp",EDGE,"E14"),sQuery(id+"F4.wireOp",EDGE,"E77"),sQuery(id+"F4.wireOp",EDGE,"E80")])]});
            var Q6;
            Q6=makeQuery(id+"F5.opExtrude","SWEPT_EDGE",EDGE,{"disambiguationData":[OSD([sQuery(id+"F4.wireOp",EDGE,"E78"),sQuery(id+"F4.wireOp",EDGE,"E79")])]});
            var Q7;
            Q7=makeQuery(id+"F5.opExtrude","SWEPT_EDGE",EDGE,{"disambiguationData":[OSD([sQuery(id+"F0.wireOp",EDGE,"E14"),sQuery(id+"F4.wireOp",EDGE,"E79"),sQuery(id+"F4.wireOp",EDGE,"E80")])]});
            var Q8;
            Q8=makeQuery(id+"F5.opExtrude","SWEPT_EDGE",EDGE,{"disambiguationData":[OSD([sQuery(id+"F4.wireOp",EDGE,"E111.MirrorCS"),sQuery(id+"F4.wireOp",EDGE,"E112.MirrorCS")])]});
            var Q9;
            Q9=makeQuery(id+"F5.opExtrude","SWEPT_EDGE",EDGE,{"disambiguationData":[OSD([sQuery(id+"F4.wireOp",EDGE,"E110.MirrorCS"),sQuery(id+"F4.wireOp",EDGE,"E111.MirrorCS")])]});
            var Q10;
            Q10=makeQuery(id+"F5.opExtrude","SWEPT_EDGE",EDGE,{"disambiguationData":[OSD([sQuery(id+"F0.wireOp",EDGE,"E56.MirrorCS"),sQuery(id+"F4.wireOp",EDGE,"E109.MirrorCS"),sQuery(id+"F4.wireOp",EDGE,"E112.MirrorCS")])]});
            var Q11;
            Q11=makeQuery(id+"F5.opExtrude","SWEPT_EDGE",EDGE,{"disambiguationData":[OSD([sQuery(id+"F0.wireOp",EDGE,"E56.MirrorCS"),sQuery(id+"F4.wireOp",EDGE,"E109.MirrorCS"),sQuery(id+"F4.wireOp",EDGE,"E110.MirrorCS")])]});
            var Q12;
            Q12=makeQuery(id+"F5.opExtrude","SWEPT_EDGE",EDGE,{"disambiguationData":[OSD([sQuery(id+"F4.wireOp",EDGE,"E132.MirrorCS"),sQuery(id+"F4.wireOp",EDGE,"E139.MirrorCS")])]});
            var Q13;
            Q13=makeQuery(id+"F5.opExtrude","SWEPT_EDGE",EDGE,{"disambiguationData":[OSD([sQuery(id+"F4.wireOp",EDGE,"E129.MirrorCS"),sQuery(id+"F4.wireOp",EDGE,"E132.MirrorCS")])]});
            var Q14;
            Q14=makeQuery(id+"F5.opExtrude","SWEPT_EDGE",EDGE,{"disambiguationData":[OSD([sQuery(id+"F0.wireOp",EDGE,"E43.MirrorCS"),sQuery(id+"F4.wireOp",EDGE,"E125.MirrorCS"),sQuery(id+"F4.wireOp",EDGE,"E129.MirrorCS")])]});
            var Q15;
            Q15=makeQuery(id+"F5.opExtrude","SWEPT_EDGE",EDGE,{"disambiguationData":[OSD([sQuery(id+"F0.wireOp",EDGE,"E43.MirrorCS"),sQuery(id+"F4.wireOp",EDGE,"E125.MirrorCS"),sQuery(id+"F4.wireOp",EDGE,"E139.MirrorCS")])]});
            var Q16;
            Q16=makeQuery(id+"F5.opExtrude","SWEPT_EDGE",EDGE,{"disambiguationData":[OSD([sQuery(id+"F4.wireOp",EDGE,"E131.MirrorCS"),sQuery(id+"F4.wireOp",EDGE,"E136.MirrorCS")])]});
            var Q17;
            Q17=makeQuery(id+"F5.opExtrude","SWEPT_EDGE",EDGE,{"disambiguationData":[OSD([sQuery(id+"F4.wireOp",EDGE,"E130.MirrorCS"),sQuery(id+"F4.wireOp",EDGE,"E131.MirrorCS")])]});
            var Q18;
            Q18=makeQuery(id+"F5.opExtrude","SWEPT_EDGE",EDGE,{"disambiguationData":[OSD([sQuery(id+"F0.wireOp",EDGE,"E48.MirrorCS"),sQuery(id+"F4.wireOp",EDGE,"E128.MirrorCS"),sQuery(id+"F4.wireOp",EDGE,"E130.MirrorCS")])]});
            var Q19;
            Q19=makeQuery(id+"F5.opExtrude","SWEPT_EDGE",EDGE,{"disambiguationData":[OSD([sQuery(id+"F0.wireOp",EDGE,"E48.MirrorCS"),sQuery(id+"F4.wireOp",EDGE,"E128.MirrorCS"),sQuery(id+"F4.wireOp",EDGE,"E136.MirrorCS")])]});
            var Q20;
            Q20=makeQuery(id+"F5.opExtrude","SWEPT_EDGE",EDGE,{"disambiguationData":[OSD([sQuery(id+"F4.wireOp",EDGE,"E92.MirrorCS"),sQuery(id+"F4.wireOp",EDGE,"E93.MirrorCS")])]});
            var Q21;
            Q21=makeQuery(id+"F5.opExtrude","SWEPT_EDGE",EDGE,{"disambiguationData":[OSD([sQuery(id+"F4.wireOp",EDGE,"E86.MirrorCS"),sQuery(id+"F4.wireOp",EDGE,"E90.MirrorCS")])]});
            var Q22;
            Q22=makeQuery(id+"F5.opExtrude","SWEPT_EDGE",EDGE,{"disambiguationData":[OSD([sQuery(id+"F4.wireOp",EDGE,"E93.MirrorCS"),sQuery(id+"F4.wireOp",EDGE,"E104.MirrorCS")])]});
            var Q23;
            Q23=makeQuery(id+"F5.opExtrude","SWEPT_EDGE",EDGE,{"disambiguationData":[OSD([sQuery(id+"F0.wireOp",EDGE,"E26.MirrorCS"),sQuery(id+"F4.wireOp",EDGE,"E102.MirrorCS"),sQuery(id+"F4.wireOp",EDGE,"E104.MirrorCS")])]});
            var Q24;
            Q24=makeQuery(id+"F5.opExtrude","SWEPT_EDGE",EDGE,{"disambiguationData":[OSD([sQuery(id+"F4.wireOp",EDGE,"E86.MirrorCS"),sQuery(id+"F4.wireOp",EDGE,"E89.MirrorCS")])]});
            var Q25;
            Q25=makeQuery(id+"F5.opExtrude","SWEPT_EDGE",EDGE,{"disambiguationData":[OSD([sQuery(id+"F0.wireOp",EDGE,"E26.MirrorCS"),sQuery(id+"F4.wireOp",EDGE,"E92.MirrorCS"),sQuery(id+"F4.wireOp",EDGE,"E102.MirrorCS")])]});
            var Q26;
            Q26=makeQuery(id+"F5.opExtrude","SWEPT_EDGE",EDGE,{"disambiguationData":[OSD([sQuery(id+"F0.wireOp",EDGE,"E28.MirrorCS"),sQuery(id+"F4.wireOp",EDGE,"E85.MirrorCS"),sQuery(id+"F4.wireOp",EDGE,"E90.MirrorCS")])]});
            var Q27;
            Q27=makeQuery(id+"F5.opExtrude","SWEPT_EDGE",EDGE,{"disambiguationData":[OSD([sQuery(id+"F0.wireOp",EDGE,"E28.MirrorCS"),sQuery(id+"F4.wireOp",EDGE,"E85.MirrorCS"),sQuery(id+"F4.wireOp",EDGE,"E89.MirrorCS")])]});
            var Q28;
            Q28=makeQuery(id+"F5.opExtrude","SWEPT_EDGE",EDGE,{"disambiguationData":[OSD([sQuery(id+"F4.wireOp",EDGE,"E120.MirrorCS"),sQuery(id+"F4.wireOp",EDGE,"E121.MirrorCS")])]});
            var Q29;
            Q29=makeQuery(id+"F5.opExtrude","SWEPT_EDGE",EDGE,{"disambiguationData":[OSD([sQuery(id+"F4.wireOp",EDGE,"E119.MirrorCS"),sQuery(id+"F4.wireOp",EDGE,"E120.MirrorCS")])]});
            var Q30;
            Q30=makeQuery(id+"F5.opExtrude","SWEPT_EDGE",EDGE,{"disambiguationData":[OSD([sQuery(id+"F0.wireOp",EDGE,"E59.MirrorCS"),sQuery(id+"F4.wireOp",EDGE,"E117.MirrorCS"),sQuery(id+"F4.wireOp",EDGE,"E121.MirrorCS")])]});
            var Q31;
            Q31=makeQuery(id+"F5.opExtrude","SWEPT_EDGE",EDGE,{"disambiguationData":[OSD([sQuery(id+"F0.wireOp",EDGE,"E59.MirrorCS"),sQuery(id+"F4.wireOp",EDGE,"E117.MirrorCS"),sQuery(id+"F4.wireOp",EDGE,"E119.MirrorCS")])]});
            var Q32;
            Q32=makeQuery(id+"F2.opShell","TWEAK_EDGE",EDGE,{"derivedFrom":[makeQuery(id+"F1.opExtrude","SWEPT_FACE",FACE,{"disambiguationData":[OSD([sQuery(id+"F0.wireOp",EDGE,"E2.bottom")])]}),makeQuery(id+"F1.opExtrude","SWEPT_FACE",FACE,{"disambiguationData":[OSD([sQuery(id+"F0.wireOp",EDGE,"E48.MirrorCS")])]})]});
            var Q33;
            Q33=makeQuery(id+"F2.opShell","TWEAK_EDGE",EDGE,{"derivedFrom":[makeQuery(id+"F1.opExtrude","SWEPT_FACE",FACE,{"disambiguationData":[OSD([sQuery(id+"F0.wireOp",EDGE,"E2.bottom")])]}),makeQuery(id+"F1.opExtrude","SWEPT_FACE",FACE,{"disambiguationData":[OSD([sQuery(id+"F0.wireOp",EDGE,"E43.MirrorCS")])]})]});
            var Q34;
            Q34=makeQuery(id+"F2.opShell","TWEAK_EDGE",EDGE,{"derivedFrom":[makeQuery(id+"F1.opExtrude","SWEPT_FACE",FACE,{"disambiguationData":[OSD([sQuery(id+"F0.wireOp",EDGE,"E23.MirrorCS")])]}),makeQuery(id+"F1.opExtrude","SWEPT_FACE",FACE,{"disambiguationData":[OSD([sQuery(id+"F0.wireOp",EDGE,"E68.trimOffspring")])]})]});
            var Q35;
            Q35=makeQuery(id+"F2.opShell","TWEAK_EDGE",EDGE,{"derivedFrom":[makeQuery(id+"F1.opExtrude","SWEPT_FACE",FACE,{"disambiguationData":[OSD([sQuery(id+"F0.wireOp",EDGE,"E2.left")])]}),makeQuery(id+"F1.opExtrude","SWEPT_FACE",FACE,{"disambiguationData":[OSD([sQuery(id+"F0.wireOp",EDGE,"E14")])]})]});
            var Q36;
            Q36=makeQuery(id+"F2.opShell","TWEAK_EDGE",EDGE,{"derivedFrom":[makeQuery(id+"F1.opExtrude","SWEPT_FACE",FACE,{"disambiguationData":[OSD([sQuery(id+"F0.wireOp",EDGE,"E2.top")])]}),makeQuery(id+"F1.opExtrude","SWEPT_FACE",FACE,{"disambiguationData":[OSD([sQuery(id+"F0.wireOp",EDGE,"E56.MirrorCS")])]})]});
            var Q37;
            Q37=makeQuery(id+"F2.opShell","TWEAK_EDGE",EDGE,{"derivedFrom":[makeQuery(id+"F1.opExtrude","SWEPT_FACE",FACE,{"disambiguationData":[OSD([sQuery(id+"F0.wireOp",EDGE,"E2.top")])]}),makeQuery(id+"F1.opExtrude","SWEPT_FACE",FACE,{"disambiguationData":[OSD([sQuery(id+"F0.wireOp",EDGE,"E59.MirrorCS")])]})]});
            var Q38;
            Q38=makeQuery(id+"F2.opShell","TWEAK_EDGE",EDGE,{"derivedFrom":[makeQuery(id+"F1.opExtrude","SWEPT_FACE",FACE,{"disambiguationData":[OSD([sQuery(id+"F0.wireOp",EDGE,"E2.right")])]}),makeQuery(id+"F1.opExtrude","SWEPT_FACE",FACE,{"disambiguationData":[OSD([sQuery(id+"F0.wireOp",EDGE,"E28.MirrorCS")])]})]});
            var Q39;
            Q39=makeQuery(id+"F2.opShell","TWEAK_EDGE",EDGE,{"derivedFrom":[makeQuery(id+"F1.opExtrude","SWEPT_FACE",FACE,{"disambiguationData":[OSD([sQuery(id+"F0.wireOp",EDGE,"E2.right")])]}),makeQuery(id+"F1.opExtrude","SWEPT_FACE",FACE,{"disambiguationData":[OSD([sQuery(id+"F0.wireOp",EDGE,"E26.MirrorCS")])]})]});
            fillet(context, id + "F11", {"entities" : qUnion([Q0, Q1, Q2, Q3, Q4, Q5, Q6, Q7, Q8, Q9, Q10, Q11, Q12, Q13, Q14, Q15, Q16, Q17, Q18, Q19, Q20, Q21, Q22, Q23, Q24, Q25, Q26, Q27, Q28, Q29, Q30, Q31, Q32, Q33, Q34, Q35, Q36, Q37, Q38, Q39]), "radius" : 2 * mm, "tangentPropagation" : true, "allowEdgeOverflow" : false});
        }
        {
            var Q0;
            Q0=makeQuery(id+"F5.opExtrude","SWEPT_EDGE",EDGE,{"disambiguationData":[OSD([sQuery(id+"F4.wireOp",EDGE,"E84.MirrorCS"),sQuery(id+"F4.wireOp",EDGE,"E87.MirrorCS")])]});
            var Q1;
            Q1=makeQuery(id+"F5.opExtrude","SWEPT_EDGE",EDGE,{"disambiguationData":[OSD([sQuery(id+"F4.wireOp",EDGE,"E84.MirrorCS"),sQuery(id+"F4.wireOp",EDGE,"E88.MirrorCS")])]});
            var Q2;
            Q2=makeQuery(id+"F5.opExtrude","SWEPT_EDGE",EDGE,{"disambiguationData":[OSD([sQuery(id+"F4.wireOp",EDGE,"E122.MirrorCS"),sQuery(id+"F4.wireOp",EDGE,"E123.MirrorCS")])]});
            var Q3;
            Q3=makeQuery(id+"F5.opExtrude","SWEPT_EDGE",EDGE,{"disambiguationData":[OSD([sQuery(id+"F4.wireOp",EDGE,"E118.MirrorCS"),sQuery(id+"F4.wireOp",EDGE,"E122.MirrorCS")])]});
            var Q4;
            Q4=makeQuery(id+"F5.opExtrude","SWEPT_EDGE",EDGE,{"disambiguationData":[OSD([sQuery(id+"F4.wireOp",EDGE,"E113.MirrorCS"),sQuery(id+"F4.wireOp",EDGE,"E116.MirrorCS")])]});
            var Q5;
            Q5=makeQuery(id+"F5.opExtrude","SWEPT_EDGE",EDGE,{"disambiguationData":[OSD([sQuery(id+"F4.wireOp",EDGE,"E113.MirrorCS"),sQuery(id+"F4.wireOp",EDGE,"E115.MirrorCS")])]});
            var Q6;
            Q6=makeQuery(id+"F5.opExtrude","SWEPT_EDGE",EDGE,{"disambiguationData":[OSD([sQuery(id+"F4.wireOp",EDGE,"E76.top"),sQuery(id+"F4.wireOp",EDGE,"E76.right")])]});
            var Q7;
            Q7=makeQuery(id+"F5.opExtrude","SWEPT_EDGE",EDGE,{"disambiguationData":[OSD([sQuery(id+"F4.wireOp",EDGE,"E76.bottom"),sQuery(id+"F4.wireOp",EDGE,"E76.right")])]});
            var Q8;
            Q8=makeQuery(id+"F5.opExtrude","SWEPT_EDGE",EDGE,{"disambiguationData":[OSD([sQuery(id+"F4.wireOp",EDGE,"E96.MirrorCS"),sQuery(id+"F4.wireOp",EDGE,"E99.MirrorCS")])]});
            var Q9;
            Q9=makeQuery(id+"F5.opExtrude","SWEPT_EDGE",EDGE,{"disambiguationData":[OSD([sQuery(id+"F4.wireOp",EDGE,"E97.MirrorCS"),sQuery(id+"F4.wireOp",EDGE,"E99.MirrorCS")])]});
            var Q10;
            Q10=makeQuery(id+"F5.opExtrude","SWEPT_EDGE",EDGE,{"disambiguationData":[OSD([sQuery(id+"F4.wireOp",EDGE,"E127.MirrorCS"),sQuery(id+"F4.wireOp",EDGE,"E138.MirrorCS")])]});
            var Q11;
            Q11=makeQuery(id+"F5.opExtrude","SWEPT_EDGE",EDGE,{"disambiguationData":[OSD([sQuery(id+"F4.wireOp",EDGE,"E138.MirrorCS"),sQuery(id+"F4.wireOp",EDGE,"E140.MirrorCS")])]});
            var Q12;
            Q12=makeQuery(id+"F5.opExtrude","SWEPT_EDGE",EDGE,{"disambiguationData":[OSD([sQuery(id+"F4.wireOp",EDGE,"E134.MirrorCS"),sQuery(id+"F4.wireOp",EDGE,"E137.MirrorCS")])]});
            var Q13;
            Q13=makeQuery(id+"F5.opExtrude","SWEPT_EDGE",EDGE,{"disambiguationData":[OSD([sQuery(id+"F4.wireOp",EDGE,"E126.MirrorCS"),sQuery(id+"F4.wireOp",EDGE,"E137.MirrorCS")])]});
            var Q14;
            Q14=makeQuery(id+"F5.opExtrude","SWEPT_EDGE",EDGE,{"disambiguationData":[OSD([sQuery(id+"F4.wireOp",EDGE,"E95.MirrorCS"),sQuery(id+"F4.wireOp",EDGE,"E103.MirrorCS")])]});
            var Q15;
            Q15=makeQuery(id+"F5.opExtrude","SWEPT_EDGE",EDGE,{"disambiguationData":[OSD([sQuery(id+"F4.wireOp",EDGE,"E94.MirrorCS"),sQuery(id+"F4.wireOp",EDGE,"E103.MirrorCS")])]});
            fillet(context, id + "F12", {"entities" : qUnion([Q0, Q1, Q2, Q3, Q4, Q5, Q6, Q7, Q8, Q9, Q10, Q11, Q12, Q13, Q14, Q15]), "radius" : 1 * mm, "tangentPropagation" : true, "allowEdgeOverflow" : false});
        }
        {
            var Q0;
            Q0=makeQuery(id+"F5.opExtrude","SWEPT_EDGE",EDGE,{"disambiguationData":[OSD([sQuery(id+"F0.wireOp",EDGE,"E58.MirrorCS"),sQuery(id+"F4.wireOp",EDGE,"E114.MirrorCS"),sQuery(id+"F4.wireOp",EDGE,"E115.MirrorCS")])]});
            var Q1;
            Q1=makeQuery(id+"F5.opExtrude","SWEPT_EDGE",EDGE,{"disambiguationData":[OSD([sQuery(id+"F0.wireOp",EDGE,"E15"),sQuery(id+"F4.wireOp",EDGE,"E76.bottom"),sQuery(id+"F4.wireOp",EDGE,"E76.left")])]});
            var Q2;
            Q2=makeQuery(id+"F5.opExtrude","SWEPT_EDGE",EDGE,{"disambiguationData":[OSD([sQuery(id+"F0.wireOp",EDGE,"E23.MirrorCS"),sQuery(id+"F4.wireOp",EDGE,"E96.MirrorCS"),sQuery(id+"F4.wireOp",EDGE,"E98.MirrorCS")])]});
            var Q3;
            Q3=makeQuery(id+"F5.opExtrude","SWEPT_EDGE",EDGE,{"disambiguationData":[OSD([sQuery(id+"F0.wireOp",EDGE,"E40.MirrorCS"),sQuery(id+"F4.wireOp",EDGE,"E135.MirrorCS"),sQuery(id+"F4.wireOp",EDGE,"E140.MirrorCS")])]});
            var Q4;
            Q4=makeQuery(id+"F5.opExtrude","SWEPT_EDGE",EDGE,{"disambiguationData":[OSD([sQuery(id+"F0.wireOp",EDGE,"E52.MirrorCS"),sQuery(id+"F4.wireOp",EDGE,"E133.MirrorCS"),sQuery(id+"F4.wireOp",EDGE,"E134.MirrorCS")])]});
            var Q5;
            Q5=makeQuery(id+"F5.opExtrude","SWEPT_EDGE",EDGE,{"disambiguationData":[OSD([sQuery(id+"F0.wireOp",EDGE,"E35.MirrorCS"),sQuery(id+"F4.wireOp",EDGE,"E94.MirrorCS"),sQuery(id+"F4.wireOp",EDGE,"E107.MirrorCS")])]});
            var Q6;
            Q6=makeQuery(id+"F5.opExtrude","SWEPT_EDGE",EDGE,{"disambiguationData":[OSD([sQuery(id+"F0.wireOp",EDGE,"E25.MirrorCS"),sQuery(id+"F4.wireOp",EDGE,"E83.MirrorCS"),sQuery(id+"F4.wireOp",EDGE,"E87.MirrorCS")])]});
            var Q7;
            Q7=makeQuery(id+"F5.opExtrude","SWEPT_EDGE",EDGE,{"disambiguationData":[OSD([sQuery(id+"F0.wireOp",EDGE,"E64.MirrorCS"),sQuery(id+"F4.wireOp",EDGE,"E123.MirrorCS"),sQuery(id+"F4.wireOp",EDGE,"E124.MirrorCS")])]});
            var Q8;
            Q8=makeQuery(id+"F2.opShell","TWEAK_EDGE",EDGE,{"derivedFrom":[makeQuery(id+"F1.opExtrude","SWEPT_FACE",FACE,{"disambiguationData":[OSD([sQuery(id+"F0.wireOp",EDGE,"E15")])]}),makeQuery(id+"F1.opExtrude","SWEPT_FACE",FACE,{"disambiguationData":[OSD([sQuery(id+"F0.wireOp",EDGE,"E75.trimOffspring")])]})]});
            var Q9;
            Q9=makeQuery(id+"F2.opShell","TWEAK_EDGE",EDGE,{"derivedFrom":[makeQuery(id+"F1.opExtrude","SWEPT_FACE",FACE,{"disambiguationData":[OSD([sQuery(id+"F0.wireOp",EDGE,"E9.MirrorCS")])]}),makeQuery(id+"F1.opExtrude","SWEPT_FACE",FACE,{"disambiguationData":[OSD([sQuery(id+"F0.wireOp",EDGE,"E58.MirrorCS")])]})]});
            var Q10;
            Q10=makeQuery(id+"F2.opShell","TWEAK_EDGE",EDGE,{"derivedFrom":[makeQuery(id+"F1.opExtrude","SWEPT_FACE",FACE,{"disambiguationData":[OSD([sQuery(id+"F0.wireOp",EDGE,"E23.MirrorCS")])]}),makeQuery(id+"F1.opExtrude","SWEPT_FACE",FACE,{"disambiguationData":[OSD([sQuery(id+"F0.wireOp",EDGE,"E68.trimOffspring")])]})]});
            var Q11;
            Q11=makeQuery(id+"F2.opShell","TWEAK_EDGE",EDGE,{"derivedFrom":[makeQuery(id+"F1.opExtrude","SWEPT_FACE",FACE,{"disambiguationData":[OSD([sQuery(id+"F0.wireOp",EDGE,"E4")])]}),makeQuery(id+"F1.opExtrude","SWEPT_FACE",FACE,{"disambiguationData":[OSD([sQuery(id+"F0.wireOp",EDGE,"E40.MirrorCS")])]})]});
            var Q12;
            Q12=makeQuery(id+"F2.opShell","TWEAK_EDGE",EDGE,{"derivedFrom":[makeQuery(id+"F1.opExtrude","SWEPT_FACE",FACE,{"disambiguationData":[OSD([sQuery(id+"F0.wireOp",EDGE,"E6.MirrorCS")])]}),makeQuery(id+"F1.opExtrude","SWEPT_FACE",FACE,{"disambiguationData":[OSD([sQuery(id+"F0.wireOp",EDGE,"E52.MirrorCS")])]})]});
            var Q13;
            Q13=makeQuery(id+"F2.opShell","TWEAK_EDGE",EDGE,{"derivedFrom":[makeQuery(id+"F1.opExtrude","SWEPT_FACE",FACE,{"disambiguationData":[OSD([sQuery(id+"F0.wireOp",EDGE,"E35.MirrorCS")])]}),makeQuery(id+"F1.opExtrude","SWEPT_FACE",FACE,{"disambiguationData":[OSD([sQuery(id+"F0.wireOp",EDGE,"E71.trimOffspring")])]})]});
            var Q14;
            Q14=makeQuery(id+"F2.opShell","TWEAK_EDGE",EDGE,{"derivedFrom":[makeQuery(id+"F1.opExtrude","SWEPT_FACE",FACE,{"disambiguationData":[OSD([sQuery(id+"F0.wireOp",EDGE,"E25.MirrorCS")])]}),makeQuery(id+"F1.opExtrude","SWEPT_FACE",FACE,{"disambiguationData":[OSD([sQuery(id+"F0.wireOp",EDGE,"E72.trimOffspring")])]})]});
            var Q15;
            Q15=makeQuery(id+"F2.opShell","TWEAK_EDGE",EDGE,{"derivedFrom":[makeQuery(id+"F1.opExtrude","SWEPT_FACE",FACE,{"disambiguationData":[OSD([sQuery(id+"F0.wireOp",EDGE,"E7.MirrorCS")])]}),makeQuery(id+"F1.opExtrude","SWEPT_FACE",FACE,{"disambiguationData":[OSD([sQuery(id+"F0.wireOp",EDGE,"E64.MirrorCS")])]})]});
            fillet(context, id + "F13", {"entities" : qUnion([Q0, Q1, Q2, Q3, Q4, Q5, Q6, Q7, Q8, Q9, Q10, Q11, Q12, Q13, Q14, Q15]), "radius" : 2 * mm, "tangentPropagation" : true, "allowEdgeOverflow" : false});
        }
        {
            var Q0;
            Q0=makeQuery(id+"F5.opExtrude","SWEPT_EDGE",EDGE,{"disambiguationData":[OSD([sQuery(id+"F4.wireOp",EDGE,"E151.MirrorCS"),sQuery(id+"F4.wireOp",EDGE,"E149.MirrorCS")])]});
            var Q1;
            Q1=makeQuery(id+"F5.opExtrude","SWEPT_EDGE",EDGE,{"disambiguationData":[OSD([sQuery(id+"F4.wireOp",EDGE,"E152.MirrorCS"),sQuery(id+"F4.wireOp",EDGE,"E149.MirrorCS")])]});
            var Q2;
            Q2=makeQuery(id+"F5.opExtrude","SWEPT_EDGE",EDGE,{"disambiguationData":[OSD([sQuery(id+"F4.wireOp",EDGE,"E152.MirrorCS"),sQuery(id+"F4.wireOp",EDGE,"E150.MirrorCS")])]});
            var Q3;
            Q3=makeQuery(id+"F5.opExtrude","SWEPT_EDGE",EDGE,{"disambiguationData":[OSD([sQuery(id+"F4.wireOp",EDGE,"E151.MirrorCS"),sQuery(id+"F4.wireOp",EDGE,"E150.MirrorCS")])]});
            var Q4;
            Q4=makeQuery(id+"F5.opExtrude","SWEPT_EDGE",EDGE,{"disambiguationData":[OSD([sQuery(id+"F4.wireOp",EDGE,"E156.MirrorCS"),sQuery(id+"F4.wireOp",EDGE,"E161.MirrorCS")])]});
            var Q5;
            Q5=makeQuery(id+"F5.opExtrude","SWEPT_EDGE",EDGE,{"disambiguationData":[OSD([sQuery(id+"F4.wireOp",EDGE,"E156.MirrorCS"),sQuery(id+"F4.wireOp",EDGE,"E162.MirrorCS")])]});
            var Q6;
            Q6=makeQuery(id+"F5.opExtrude","SWEPT_EDGE",EDGE,{"disambiguationData":[OSD([sQuery(id+"F4.wireOp",EDGE,"E155.MirrorCS"),sQuery(id+"F4.wireOp",EDGE,"E161.MirrorCS")])]});
            var Q7;
            Q7=makeQuery(id+"F5.opExtrude","SWEPT_EDGE",EDGE,{"disambiguationData":[OSD([sQuery(id+"F4.wireOp",EDGE,"E155.MirrorCS"),sQuery(id+"F4.wireOp",EDGE,"E162.MirrorCS")])]});
            var Q8;
            Q8=makeQuery(id+"F5.opExtrude","SWEPT_EDGE",EDGE,{"disambiguationData":[OSD([sQuery(id+"F4.wireOp",EDGE,"E159.MirrorCS"),sQuery(id+"F4.wireOp",EDGE,"E163.MirrorCS")])]});
            var Q9;
            Q9=makeQuery(id+"F5.opExtrude","SWEPT_EDGE",EDGE,{"disambiguationData":[OSD([sQuery(id+"F4.wireOp",EDGE,"E160.MirrorCS"),sQuery(id+"F4.wireOp",EDGE,"E163.MirrorCS")])]});
            var Q10;
            Q10=makeQuery(id+"F5.opExtrude","SWEPT_EDGE",EDGE,{"disambiguationData":[OSD([sQuery(id+"F4.wireOp",EDGE,"E160.MirrorCS"),sQuery(id+"F4.wireOp",EDGE,"E164.MirrorCS")])]});
            var Q11;
            Q11=makeQuery(id+"F5.opExtrude","SWEPT_EDGE",EDGE,{"disambiguationData":[OSD([sQuery(id+"F4.wireOp",EDGE,"E159.MirrorCS"),sQuery(id+"F4.wireOp",EDGE,"E164.MirrorCS")])]});
            var Q12;
            Q12=makeQuery(id+"F5.opExtrude","SWEPT_EDGE",EDGE,{"disambiguationData":[OSD([sQuery(id+"F4.wireOp",EDGE,"E142.0"),sQuery(id+"F4.wireOp",EDGE,"E145")])]});
            var Q13;
            Q13=makeQuery(id+"F5.opExtrude","SWEPT_EDGE",EDGE,{"disambiguationData":[OSD([sQuery(id+"F4.wireOp",EDGE,"E141"),sQuery(id+"F4.wireOp",EDGE,"E145")])]});
            var Q14;
            Q14=makeQuery(id+"F5.opExtrude","SWEPT_EDGE",EDGE,{"disambiguationData":[OSD([sQuery(id+"F4.wireOp",EDGE,"E142.0"),sQuery(id+"F4.wireOp",EDGE,"E146")])]});
            var Q15;
            Q15=makeQuery(id+"F5.opExtrude","SWEPT_EDGE",EDGE,{"disambiguationData":[OSD([sQuery(id+"F4.wireOp",EDGE,"E141"),sQuery(id+"F4.wireOp",EDGE,"E146")])]});
            fillet(context, id + "F14", {"entities" : qUnion([Q0, Q1, Q2, Q3, Q4, Q5, Q6, Q7, Q8, Q9, Q10, Q11, Q12, Q13, Q14, Q15]), "radius" : 0.5 * mm, "tangentPropagation" : true, "allowEdgeOverflow" : false});
        }
        {
            var Q0;
            Q0=makeQuery(id+"F1.opExtrude","SWEPT_EDGE",EDGE,{"disambiguationData":[OSD([sQuery(id+"F0.wireOp",EDGE,"E17"),sQuery(id+"F0.wireOp",EDGE,"E75.trimOffspring")])]});
            var Q1;
            Q1=makeQuery(id+"F1.opExtrude","SWEPT_EDGE",EDGE,{"disambiguationData":[OSD([sQuery(id+"F0.wireOp",EDGE,"E16"),sQuery(id+"F0.wireOp",EDGE,"E17")])]});
            var Q2;
            Q2=makeQuery(id+"F1.opExtrude","SWEPT_EDGE",EDGE,{"disambiguationData":[OSD([sQuery(id+"F0.wireOp",EDGE,"E10.MirrorCS"),sQuery(id+"F0.wireOp",EDGE,"E11")])]});
            var Q3;
            Q3=makeQuery(id+"F1.opExtrude","SWEPT_EDGE",EDGE,{"disambiguationData":[OSD([sQuery(id+"F0.wireOp",EDGE,"E11"),sQuery(id+"F0.wireOp",EDGE,"E12")])]});
            var Q4;
            Q4=makeQuery(id+"F1.opExtrude","SWEPT_EDGE",EDGE,{"disambiguationData":[OSD([sQuery(id+"F0.wireOp",EDGE,"E61.MirrorCS"),sQuery(id+"F0.wireOp",EDGE,"E62.MirrorCS")])]});
            var Q5;
            Q5=makeQuery(id+"F1.opExtrude","SWEPT_EDGE",EDGE,{"disambiguationData":[OSD([sQuery(id+"F0.wireOp",EDGE,"E9.MirrorCS"),sQuery(id+"F0.wireOp",EDGE,"E61.MirrorCS")])]});
            var Q6;
            Q6=makeQuery(id+"F1.opExtrude","SWEPT_EDGE",EDGE,{"disambiguationData":[OSD([sQuery(id+"F0.wireOp",EDGE,"E57.MirrorCS"),sQuery(id+"F0.wireOp",EDGE,"E60.MirrorCS")])]});
            var Q7;
            Q7=makeQuery(id+"F1.opExtrude","SWEPT_EDGE",EDGE,{"disambiguationData":[OSD([sQuery(id+"F0.wireOp",EDGE,"E60.MirrorCS"),sQuery(id+"F0.wireOp",EDGE,"E74.trimOffspring")])]});
            var Q8;
            Q8=makeQuery(id+"F1.opExtrude","SWEPT_EDGE",EDGE,{"disambiguationData":[OSD([sQuery(id+"F0.wireOp",EDGE,"E55.MirrorCS"),sQuery(id+"F0.wireOp",EDGE,"E66.MirrorCS")])]});
            var Q9;
            Q9=makeQuery(id+"F1.opExtrude","SWEPT_EDGE",EDGE,{"disambiguationData":[OSD([sQuery(id+"F0.wireOp",EDGE,"E55.MirrorCS"),sQuery(id+"F0.wireOp",EDGE,"E73.trimOffspring")])]});
            var Q10;
            Q10=makeQuery(id+"F1.opExtrude","SWEPT_EDGE",EDGE,{"disambiguationData":[OSD([sQuery(id+"F0.wireOp",EDGE,"E63.MirrorCS"),sQuery(id+"F0.wireOp",EDGE,"E65.MirrorCS")])]});
            var Q11;
            Q11=makeQuery(id+"F1.opExtrude","SWEPT_EDGE",EDGE,{"disambiguationData":[OSD([sQuery(id+"F0.wireOp",EDGE,"E7.MirrorCS"),sQuery(id+"F0.wireOp",EDGE,"E63.MirrorCS")])]});
            var Q12;
            Q12=makeQuery(id+"F1.opExtrude","SWEPT_EDGE",EDGE,{"disambiguationData":[OSD([sQuery(id+"F0.wireOp",EDGE,"E8.MirrorCS"),sQuery(id+"F0.wireOp",EDGE,"E36.MirrorCS")])]});
            var Q13;
            Q13=makeQuery(id+"F1.opExtrude","SWEPT_EDGE",EDGE,{"disambiguationData":[OSD([sQuery(id+"F0.wireOp",EDGE,"E36.MirrorCS"),sQuery(id+"F0.wireOp",EDGE,"E38.MirrorCS")])]});
            var Q14;
            Q14=makeQuery(id+"F1.opExtrude","SWEPT_EDGE",EDGE,{"disambiguationData":[OSD([sQuery(id+"F0.wireOp",EDGE,"E32.MirrorCS"),sQuery(id+"F0.wireOp",EDGE,"E72.trimOffspring")])]});
            var Q15;
            Q15=makeQuery(id+"F1.opExtrude","SWEPT_EDGE",EDGE,{"disambiguationData":[OSD([sQuery(id+"F0.wireOp",EDGE,"E32.MirrorCS"),sQuery(id+"F0.wireOp",EDGE,"E37.MirrorCS")])]});
            var Q16;
            Q16=makeQuery(id+"F1.opExtrude","SWEPT_EDGE",EDGE,{"disambiguationData":[OSD([sQuery(id+"F0.wireOp",EDGE,"E29.MirrorCS"),sQuery(id+"F0.wireOp",EDGE,"E34.MirrorCS")])]});
            var Q17;
            Q17=makeQuery(id+"F1.opExtrude","SWEPT_EDGE",EDGE,{"disambiguationData":[OSD([sQuery(id+"F0.wireOp",EDGE,"E34.MirrorCS"),sQuery(id+"F0.wireOp",EDGE,"E71.trimOffspring")])]});
            var Q18;
            Q18=makeQuery(id+"F1.opExtrude","SWEPT_EDGE",EDGE,{"disambiguationData":[OSD([sQuery(id+"F0.wireOp",EDGE,"E27.MirrorCS"),sQuery(id+"F0.wireOp",EDGE,"E33.MirrorCS")])]});
            var Q19;
            Q19=makeQuery(id+"F1.opExtrude","SWEPT_EDGE",EDGE,{"disambiguationData":[OSD([sQuery(id+"F0.wireOp",EDGE,"E5.MirrorCS"),sQuery(id+"F0.wireOp",EDGE,"E33.MirrorCS")])]});
            var Q20;
            Q20=makeQuery(id+"F1.opExtrude","SWEPT_EDGE",EDGE,{"disambiguationData":[OSD([sQuery(id+"F0.wireOp",EDGE,"E47.MirrorCS"),sQuery(id+"F0.wireOp",EDGE,"E50.MirrorCS")])]});
            var Q21;
            Q21=makeQuery(id+"F1.opExtrude","SWEPT_EDGE",EDGE,{"disambiguationData":[OSD([sQuery(id+"F0.wireOp",EDGE,"E50.MirrorCS"),sQuery(id+"F0.wireOp",EDGE,"E70.trimOffspring")])]});
            var Q22;
            Q22=makeQuery(id+"F1.opExtrude","SWEPT_EDGE",EDGE,{"disambiguationData":[OSD([sQuery(id+"F0.wireOp",EDGE,"E49.MirrorCS"),sQuery(id+"F0.wireOp",EDGE,"E53.MirrorCS")])]});
            var Q23;
            Q23=makeQuery(id+"F1.opExtrude","SWEPT_EDGE",EDGE,{"disambiguationData":[OSD([sQuery(id+"F0.wireOp",EDGE,"E6.MirrorCS"),sQuery(id+"F0.wireOp",EDGE,"E53.MirrorCS")])]});
            var Q24;
            Q24=makeQuery(id+"F1.opExtrude","SWEPT_EDGE",EDGE,{"disambiguationData":[OSD([sQuery(id+"F0.wireOp",EDGE,"E45.MirrorCS"),sQuery(id+"F0.wireOp",EDGE,"E46.MirrorCS")])]});
            var Q25;
            Q25=makeQuery(id+"F1.opExtrude","SWEPT_EDGE",EDGE,{"disambiguationData":[OSD([sQuery(id+"F0.wireOp",EDGE,"E45.MirrorCS"),sQuery(id+"F0.wireOp",EDGE,"E69.trimOffspring")])]});
            var Q26;
            Q26=makeQuery(id+"F1.opExtrude","SWEPT_EDGE",EDGE,{"disambiguationData":[OSD([sQuery(id+"F0.wireOp",EDGE,"E4"),sQuery(id+"F0.wireOp",EDGE,"E42.MirrorCS")])]});
            var Q27;
            Q27=makeQuery(id+"F1.opExtrude","SWEPT_EDGE",EDGE,{"disambiguationData":[OSD([sQuery(id+"F0.wireOp",EDGE,"E41.MirrorCS"),sQuery(id+"F0.wireOp",EDGE,"E42.MirrorCS")])]});
            var Q28;
            Q28=makeQuery(id+"F1.opExtrude","SWEPT_EDGE",EDGE,{"disambiguationData":[OSD([sQuery(id+"F0.wireOp",EDGE,"E18.MirrorCS"),sQuery(id+"F0.wireOp",EDGE,"E24.MirrorCS")])]});
            var Q29;
            Q29=makeQuery(id+"F1.opExtrude","SWEPT_EDGE",EDGE,{"disambiguationData":[OSD([sQuery(id+"F0.wireOp",EDGE,"E24.MirrorCS"),sQuery(id+"F0.wireOp",EDGE,"E68.trimOffspring")])]});
            var Q30;
            Q30=makeQuery(id+"F1.opExtrude","SWEPT_EDGE",EDGE,{"disambiguationData":[OSD([sQuery(id+"F0.wireOp",EDGE,"E20.MirrorCS"),sQuery(id+"F0.wireOp",EDGE,"E22.MirrorCS")])]});
            var Q31;
            Q31=makeQuery(id+"F1.opExtrude","SWEPT_EDGE",EDGE,{"disambiguationData":[OSD([sQuery(id+"F0.wireOp",EDGE,"E3"),sQuery(id+"F0.wireOp",EDGE,"E20.MirrorCS")])]});
            fillet(context, id + "F15", {"entities" : qUnion([Q0, Q1, Q2, Q3, Q4, Q5, Q6, Q7, Q8, Q9, Q10, Q11, Q12, Q13, Q14, Q15, Q16, Q17, Q18, Q19, Q20, Q21, Q22, Q23, Q24, Q25, Q26, Q27, Q28, Q29, Q30, Q31]), "radius" : 0.5 * mm, "tangentPropagation" : true, "allowEdgeOverflow" : false});
        }
    });
